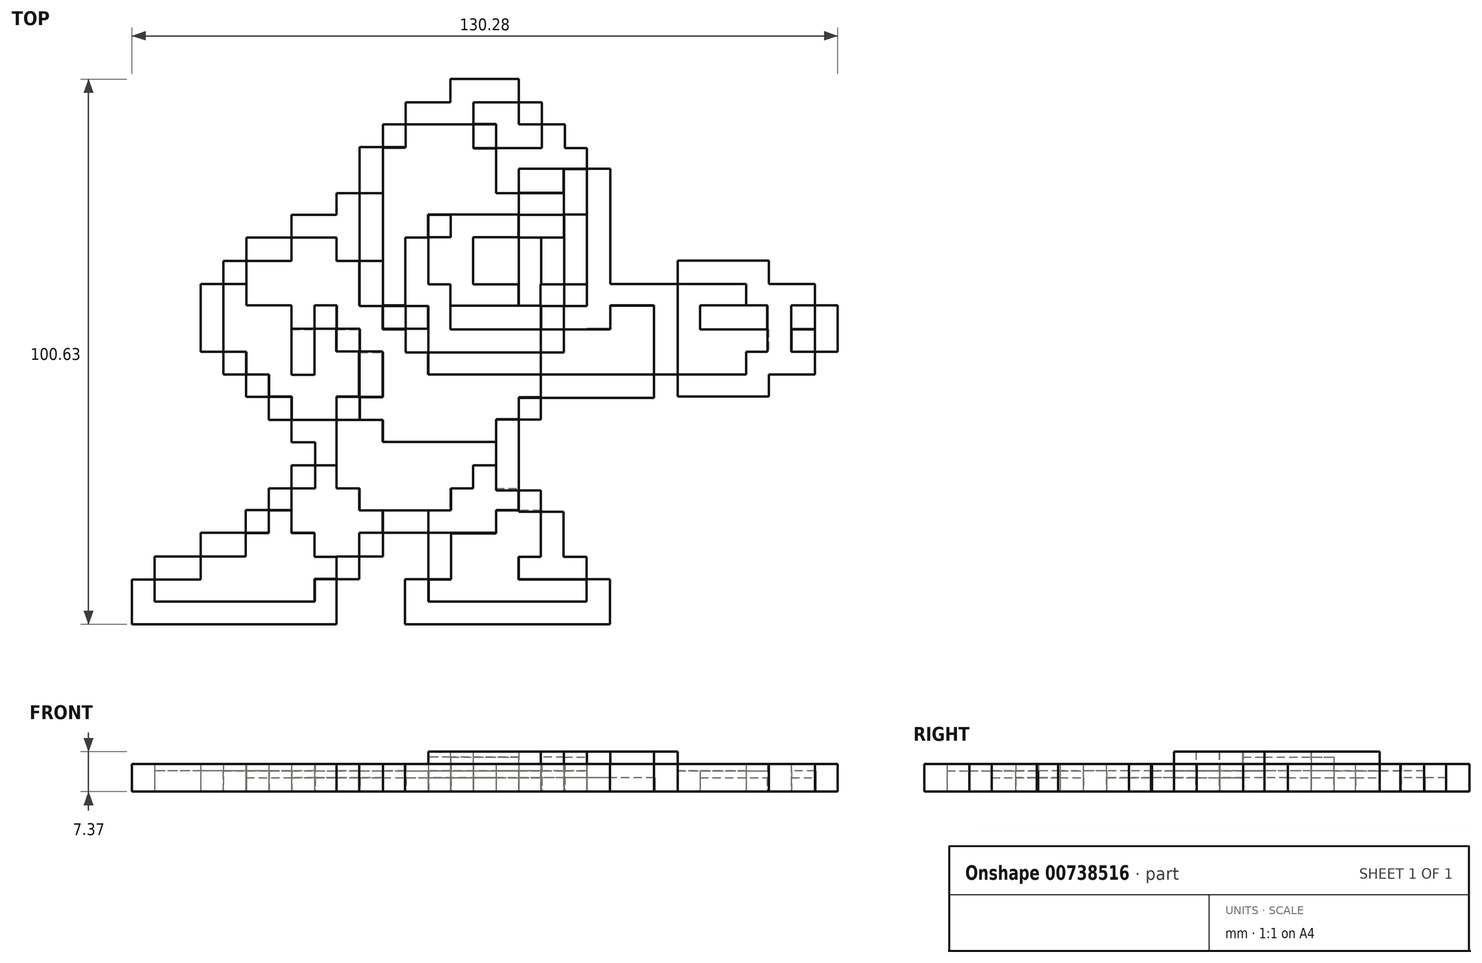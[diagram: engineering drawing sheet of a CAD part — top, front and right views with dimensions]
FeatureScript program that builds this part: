
annotation { "Feature Type Name" : "Feature", "Feature Type Description" : "" }
export const myFeature = defineFeature(function(context is Context, id is Id, definition is map)
    precondition{}
    {
        {
            var Q0;
            Q0=qCreatedBy(makeId("Top.planeOp"),FACE);
            var sketch = newSketch(context, id + "F0", { "sketchPlane" : qUnion([Q0])});
            skLineSegment(sketch, "E0.bottom", {"start": v(-1.86, 51.42) * mm, "end": v(10.8, 51.42) * mm});
            skLineSegment(sketch, "E0.top", {"start": v(-1.86, 47.1) * mm, "end": v(10.8, 47.1) * mm});
            skLineSegment(sketch, "E0.left", {"start": v(-1.86, 51.42) * mm, "end": v(-1.86, 47.1) * mm});
            skLineSegment(sketch, "E0.right", {"start": v(10.8, 51.42) * mm, "end": v(10.8, 47.1) * mm});
            skLineSegment(sketch, "E1.bottom", {"start": v(10.8, 47.1) * mm, "end": v(15.04, 47.1) * mm});
            skLineSegment(sketch, "E1.top", {"start": v(10.8, 43.08) * mm, "end": v(15.04, 43.08) * mm});
            skLineSegment(sketch, "E1.left", {"start": v(10.8, 47.1) * mm, "end": v(10.8, 43.08) * mm});
            skLineSegment(sketch, "E1.right", {"start": v(15.04, 47.1) * mm, "end": v(15.04, 43.08) * mm});
            skLineSegment(sketch, "E2.bottom", {"start": v(15.04, 43.08) * mm, "end": v(19.28, 43.08) * mm});
            skLineSegment(sketch, "E2.top", {"start": v(15.04, 38.7) * mm, "end": v(19.28, 38.7) * mm});
            skLineSegment(sketch, "E2.left", {"start": v(15.04, 43.08) * mm, "end": v(15.04, 38.7) * mm});
            skLineSegment(sketch, "E2.right", {"start": v(19.28, 43.08) * mm, "end": v(19.28, 38.7) * mm});
            skLineSegment(sketch, "E3.bottom", {"start": v(23.38, 38.7) * mm, "end": v(6.63, 38.7) * mm});
            skLineSegment(sketch, "E3.top", {"start": v(23.38, 34.9) * mm, "end": v(6.63, 34.9) * mm});
            skLineSegment(sketch, "E3.left", {"start": v(23.38, 38.7) * mm, "end": v(23.38, 34.9) * mm});
            skLineSegment(sketch, "E3.right", {"start": v(6.63, 38.7) * mm, "end": v(6.63, 34.9) * mm});
            skLineSegment(sketch, "E4.bottom", {"start": v(23.38, 34.9) * mm, "end": v(27.66, 34.9) * mm});
            skLineSegment(sketch, "E4.top", {"start": v(23.38, 5.29) * mm, "end": v(27.66, 5.29) * mm});
            skLineSegment(sketch, "E4.left", {"start": v(23.38, 34.9) * mm, "end": v(23.38, 5.29) * mm});
            skLineSegment(sketch, "E4.right", {"start": v(27.66, 34.9) * mm, "end": v(27.66, 5.29) * mm});
            skLineSegment(sketch, "E5.bottom", {"start": v(27.66, 13.62) * mm, "end": v(40.12, 13.62) * mm});
            skLineSegment(sketch, "E5.top", {"start": v(27.66, 9.67) * mm, "end": v(40.12, 9.67) * mm});
            skLineSegment(sketch, "E5.left", {"start": v(27.66, 13.62) * mm, "end": v(27.66, 9.67) * mm});
            skLineSegment(sketch, "E5.right", {"start": v(40.12, 13.62) * mm, "end": v(40.12, 9.67) * mm});
            skLineSegment(sketch, "E6.bottom", {"start": v(40.12, 13.62) * mm, "end": v(56.96, 13.62) * mm});
            skLineSegment(sketch, "E6.top", {"start": v(40.12, 17.94) * mm, "end": v(56.96, 17.94) * mm});
            skLineSegment(sketch, "E6.left", {"start": v(40.12, 13.62) * mm, "end": v(40.12, 17.94) * mm});
            skLineSegment(sketch, "E6.right", {"start": v(56.96, 13.62) * mm, "end": v(56.96, 17.94) * mm});
            skLineSegment(sketch, "E7.bottom", {"start": v(52.76, 13.62) * mm, "end": v(65.5, 13.62) * mm});
            skLineSegment(sketch, "E7.top", {"start": v(52.76, 9.65) * mm, "end": v(65.5, 9.65) * mm});
            skLineSegment(sketch, "E7.left", {"start": v(52.76, 13.62) * mm, "end": v(52.76, 9.65) * mm});
            skLineSegment(sketch, "E7.right", {"start": v(65.5, 13.62) * mm, "end": v(65.5, 9.65) * mm});
            skLineSegment(sketch, "E8.bottom", {"start": v(65.5, 9.65) * mm, "end": v(69.66, 9.65) * mm});
            skLineSegment(sketch, "E8.top", {"start": v(65.5, 1.07) * mm, "end": v(69.66, 1.07) * mm});
            skLineSegment(sketch, "E8.left", {"start": v(65.5, 9.65) * mm, "end": v(65.5, 1.07) * mm});
            skLineSegment(sketch, "E8.right", {"start": v(69.66, 9.65) * mm, "end": v(69.66, 1.07) * mm});
            skLineSegment(sketch, "E9.bottom", {"start": v(65.5, 1.07) * mm, "end": v(52.76, 1.07) * mm});
            skLineSegment(sketch, "E9.top", {"start": v(65.5, -3.1) * mm, "end": v(52.76, -3.1) * mm});
            skLineSegment(sketch, "E9.left", {"start": v(65.5, 1.07) * mm, "end": v(65.5, -3.1) * mm});
            skLineSegment(sketch, "E9.right", {"start": v(52.76, 1.07) * mm, "end": v(52.76, -3.1) * mm});
            skLineSegment(sketch, "E10.bottom", {"start": v(56.96, -3.1) * mm, "end": v(40.12, -3.1) * mm});
            skLineSegment(sketch, "E10.top", {"start": v(56.96, -7.17) * mm, "end": v(40.12, -7.17) * mm});
            skLineSegment(sketch, "E10.left", {"start": v(56.96, -3.1) * mm, "end": v(56.96, -7.17) * mm});
            skLineSegment(sketch, "E10.right", {"start": v(40.12, -3.1) * mm, "end": v(40.12, -7.17) * mm});
            skLineSegment(sketch, "E11.bottom", {"start": v(40.12, -3.1) * mm, "end": v(35.78, -3.1) * mm});
            skLineSegment(sketch, "E11.top", {"start": v(40.12, 9.67) * mm, "end": v(35.78, 9.67) * mm});
            skLineSegment(sketch, "E11.left", {"start": v(40.12, -3.1) * mm, "end": v(40.12, 9.67) * mm});
            skLineSegment(sketch, "E11.right", {"start": v(35.78, -3.1) * mm, "end": v(35.78, 9.67) * mm});
            skLineSegment(sketch, "E12.bottom", {"start": v(35.78, -3.1) * mm, "end": v(14.88, -3.1) * mm});
            skLineSegment(sketch, "E12.top", {"start": v(35.78, -7.38) * mm, "end": v(14.88, -7.38) * mm});
            skLineSegment(sketch, "E12.left", {"start": v(35.78, -3.1) * mm, "end": v(35.78, -7.38) * mm});
            skLineSegment(sketch, "E12.right", {"start": v(14.88, -3.1) * mm, "end": v(14.88, -7.38) * mm});
            skLineSegment(sketch, "E13.bottom", {"start": v(14.88, -7.38) * mm, "end": v(10.8, -7.38) * mm});
            skLineSegment(sketch, "E13.top", {"start": v(14.88, -11.41) * mm, "end": v(10.8, -11.41) * mm});
            skLineSegment(sketch, "E13.left", {"start": v(14.88, -7.38) * mm, "end": v(14.88, -11.41) * mm});
            skLineSegment(sketch, "E13.right", {"start": v(10.8, -7.38) * mm, "end": v(10.8, -11.41) * mm});
            skLineSegment(sketch, "E14.bottom", {"start": v(10.8, -11.41) * mm, "end": v(6.62, -11.41) * mm});
            skLineSegment(sketch, "E14.top", {"start": v(10.8, -24.48) * mm, "end": v(6.62, -24.48) * mm});
            skLineSegment(sketch, "E14.left", {"start": v(10.8, -11.41) * mm, "end": v(10.8, -24.48) * mm});
            skLineSegment(sketch, "E14.right", {"start": v(6.62, -11.41) * mm, "end": v(6.62, -24.48) * mm});
            skLineSegment(sketch, "E15.bottom", {"start": v(10.8, -24.48) * mm, "end": v(14.88, -24.48) * mm});
            skLineSegment(sketch, "E15.top", {"start": v(10.8, -28.42) * mm, "end": v(14.88, -28.42) * mm});
            skLineSegment(sketch, "E15.left", {"start": v(10.8, -24.48) * mm, "end": v(10.8, -28.42) * mm});
            skLineSegment(sketch, "E15.right", {"start": v(14.88, -24.48) * mm, "end": v(14.88, -28.42) * mm});
            skLineSegment(sketch, "E16.bottom", {"start": v(14.88, -28.42) * mm, "end": v(19.08, -28.42) * mm});
            skLineSegment(sketch, "E16.top", {"start": v(14.88, -40.86) * mm, "end": v(19.08, -40.86) * mm});
            skLineSegment(sketch, "E16.left", {"start": v(14.88, -28.42) * mm, "end": v(14.88, -40.86) * mm});
            skLineSegment(sketch, "E16.right", {"start": v(19.08, -28.42) * mm, "end": v(19.08, -40.86) * mm});
            skLineSegment(sketch, "E17.bottom", {"start": v(10.8, -36.74) * mm, "end": v(23.28, -36.74) * mm});
            skLineSegment(sketch, "E17.top", {"start": v(10.8, -40.86) * mm, "end": v(23.28, -40.86) * mm});
            skLineSegment(sketch, "E17.left", {"start": v(10.8, -36.74) * mm, "end": v(10.8, -40.86) * mm});
            skLineSegment(sketch, "E17.right", {"start": v(23.28, -36.74) * mm, "end": v(23.28, -40.86) * mm});
            skLineSegment(sketch, "E18.bottom", {"start": v(23.28, -40.86) * mm, "end": v(27.63, -40.86) * mm});
            skLineSegment(sketch, "E18.top", {"start": v(23.28, -49.2) * mm, "end": v(27.63, -49.2) * mm});
            skLineSegment(sketch, "E18.left", {"start": v(23.28, -40.86) * mm, "end": v(23.28, -49.2) * mm});
            skLineSegment(sketch, "E18.right", {"start": v(27.63, -40.86) * mm, "end": v(27.63, -49.2) * mm});
            skLineSegment(sketch, "E19.bottom", {"start": v(23.28, -45.03) * mm, "end": v(-10.2, -45.03) * mm});
            skLineSegment(sketch, "E19.top", {"start": v(23.28, -49.2) * mm, "end": v(-10.2, -49.2) * mm});
            skLineSegment(sketch, "E19.left", {"start": v(23.28, -45.03) * mm, "end": v(23.28, -49.2) * mm});
            skLineSegment(sketch, "E19.right", {"start": v(-10.2, -45.03) * mm, "end": v(-10.2, -49.2) * mm});
            skLineSegment(sketch, "E20.bottom", {"start": v(-10.2, -45.03) * mm, "end": v(-5.92, -45.03) * mm});
            skLineSegment(sketch, "E20.top", {"start": v(-10.2, -40.86) * mm, "end": v(-5.92, -40.86) * mm});
            skLineSegment(sketch, "E20.left", {"start": v(-10.2, -45.03) * mm, "end": v(-10.2, -40.86) * mm});
            skLineSegment(sketch, "E20.right", {"start": v(-5.92, -45.03) * mm, "end": v(-5.92, -40.86) * mm});
            skLineSegment(sketch, "E21.bottom", {"start": v(-5.92, -40.86) * mm, "end": v(-1.73, -40.86) * mm});
            skLineSegment(sketch, "E21.top", {"start": v(-5.92, -32.3) * mm, "end": v(-1.73, -32.3) * mm});
            skLineSegment(sketch, "E21.left", {"start": v(-5.92, -40.86) * mm, "end": v(-5.92, -32.3) * mm});
            skLineSegment(sketch, "E21.right", {"start": v(-1.73, -40.86) * mm, "end": v(-1.73, -32.3) * mm});
            skLineSegment(sketch, "E22.bottom", {"start": v(-5.92, -32.3) * mm, "end": v(-14.29, -32.3) * mm});
            skLineSegment(sketch, "E22.top", {"start": v(-5.92, -28.2) * mm, "end": v(-14.29, -28.2) * mm});
            skLineSegment(sketch, "E22.left", {"start": v(-5.92, -32.3) * mm, "end": v(-5.92, -28.2) * mm});
            skLineSegment(sketch, "E22.right", {"start": v(-14.29, -32.3) * mm, "end": v(-14.29, -28.2) * mm});
            skLineSegment(sketch, "E23.bottom", {"start": v(-14.29, -32.3) * mm, "end": v(-18.67, -32.3) * mm});
            skLineSegment(sketch, "E23.top", {"start": v(-14.29, -36.7) * mm, "end": v(-18.67, -36.7) * mm});
            skLineSegment(sketch, "E23.left", {"start": v(-14.29, -32.3) * mm, "end": v(-14.29, -36.7) * mm});
            skLineSegment(sketch, "E23.right", {"start": v(-18.67, -32.3) * mm, "end": v(-18.67, -36.7) * mm});
            skLineSegment(sketch, "E24.bottom", {"start": v(-18.67, -36.7) * mm, "end": v(-22.84, -36.7) * mm});
            skLineSegment(sketch, "E24.top", {"start": v(-18.67, -40.86) * mm, "end": v(-22.84, -40.86) * mm});
            skLineSegment(sketch, "E24.left", {"start": v(-18.67, -36.7) * mm, "end": v(-18.67, -40.86) * mm});
            skLineSegment(sketch, "E24.right", {"start": v(-22.84, -36.7) * mm, "end": v(-22.84, -40.86) * mm});
            skLineSegment(sketch, "E25.bottom", {"start": v(-22.84, -40.86) * mm, "end": v(-26.85, -40.86) * mm});
            skLineSegment(sketch, "E25.top", {"start": v(-22.84, -49.2) * mm, "end": v(-26.85, -49.2) * mm});
            skLineSegment(sketch, "E25.left", {"start": v(-22.84, -40.86) * mm, "end": v(-22.84, -49.2) * mm});
            skLineSegment(sketch, "E25.right", {"start": v(-26.85, -40.86) * mm, "end": v(-26.85, -49.2) * mm});
            skLineSegment(sketch, "E26.bottom", {"start": v(-26.85, -49.2) * mm, "end": v(-60.62, -49.2) * mm});
            skLineSegment(sketch, "E26.top", {"start": v(-26.85, -45.03) * mm, "end": v(-60.62, -45.03) * mm});
            skLineSegment(sketch, "E26.left", {"start": v(-26.85, -49.2) * mm, "end": v(-26.85, -45.03) * mm});
            skLineSegment(sketch, "E26.right", {"start": v(-60.62, -49.2) * mm, "end": v(-60.62, -45.03) * mm});
            skLineSegment(sketch, "E27.bottom", {"start": v(-60.62, -45.03) * mm, "end": v(-56.45, -45.03) * mm});
            skLineSegment(sketch, "E27.top", {"start": v(-60.62, -40.91) * mm, "end": v(-56.45, -40.91) * mm});
            skLineSegment(sketch, "E27.left", {"start": v(-60.62, -45.03) * mm, "end": v(-60.62, -40.91) * mm});
            skLineSegment(sketch, "E27.right", {"start": v(-56.45, -45.03) * mm, "end": v(-56.45, -40.91) * mm});
            skLineSegment(sketch, "E28.bottom", {"start": v(-56.45, -40.91) * mm, "end": v(-47.92, -40.91) * mm});
            skLineSegment(sketch, "E28.top", {"start": v(-56.45, -36.66) * mm, "end": v(-47.92, -36.66) * mm});
            skLineSegment(sketch, "E28.left", {"start": v(-56.45, -40.91) * mm, "end": v(-56.45, -36.66) * mm});
            skLineSegment(sketch, "E28.right", {"start": v(-47.92, -40.91) * mm, "end": v(-47.92, -36.66) * mm});
            skLineSegment(sketch, "E29.bottom", {"start": v(-47.92, -36.66) * mm, "end": v(-39.62, -36.66) * mm});
            skLineSegment(sketch, "E29.top", {"start": v(-47.92, -32.3) * mm, "end": v(-39.62, -32.3) * mm});
            skLineSegment(sketch, "E29.left", {"start": v(-47.92, -36.66) * mm, "end": v(-47.92, -32.3) * mm});
            skLineSegment(sketch, "E29.right", {"start": v(-39.62, -36.66) * mm, "end": v(-39.62, -32.3) * mm});
            skLineSegment(sketch, "E30.bottom", {"start": v(-39.62, -32.3) * mm, "end": v(-35.38, -32.3) * mm});
            skLineSegment(sketch, "E30.top", {"start": v(-39.62, -28.14) * mm, "end": v(-35.38, -28.14) * mm});
            skLineSegment(sketch, "E30.left", {"start": v(-39.62, -32.3) * mm, "end": v(-39.62, -28.14) * mm});
            skLineSegment(sketch, "E30.right", {"start": v(-35.38, -32.3) * mm, "end": v(-35.38, -28.14) * mm});
            skLineSegment(sketch, "E31.bottom", {"start": v(-35.38, -28.14) * mm, "end": v(-31.17, -28.14) * mm});
            skLineSegment(sketch, "E31.top", {"start": v(-35.38, -24.12) * mm, "end": v(-31.17, -24.12) * mm});
            skLineSegment(sketch, "E31.left", {"start": v(-35.38, -28.14) * mm, "end": v(-35.38, -24.12) * mm});
            skLineSegment(sketch, "E31.right", {"start": v(-31.17, -28.14) * mm, "end": v(-31.17, -24.12) * mm});
            skLineSegment(sketch, "E32.bottom", {"start": v(-31.17, -24.12) * mm, "end": v(-26.82, -24.12) * mm});
            skLineSegment(sketch, "E32.top", {"start": v(-31.17, -19.84) * mm, "end": v(-26.82, -19.84) * mm});
            skLineSegment(sketch, "E32.left", {"start": v(-31.17, -24.12) * mm, "end": v(-31.17, -19.84) * mm});
            skLineSegment(sketch, "E32.right", {"start": v(-26.82, -24.12) * mm, "end": v(-26.82, -19.84) * mm});
            skLineSegment(sketch, "E33.bottom", {"start": v(-26.82, -19.84) * mm, "end": v(-22.88, -19.84) * mm});
            skLineSegment(sketch, "E33.top", {"start": v(-26.82, -11.45) * mm, "end": v(-22.88, -11.45) * mm});
            skLineSegment(sketch, "E33.left", {"start": v(-26.82, -19.84) * mm, "end": v(-26.82, -11.45) * mm});
            skLineSegment(sketch, "E33.right", {"start": v(-22.88, -19.84) * mm, "end": v(-22.88, -11.45) * mm});
            skLineSegment(sketch, "E34.bottom", {"start": v(-26.82, -11.45) * mm, "end": v(-31.17, -11.45) * mm});
            skLineSegment(sketch, "E34.top", {"start": v(-26.82, -15.62) * mm, "end": v(-31.17, -15.62) * mm});
            skLineSegment(sketch, "E34.left", {"start": v(-26.82, -11.45) * mm, "end": v(-26.82, -15.62) * mm});
            skLineSegment(sketch, "E34.right", {"start": v(-31.17, -11.45) * mm, "end": v(-31.17, -15.62) * mm});
            skLineSegment(sketch, "E35.bottom", {"start": v(-31.17, -11.45) * mm, "end": v(-35.39, -11.45) * mm});
            skLineSegment(sketch, "E35.top", {"start": v(-31.17, -7.24) * mm, "end": v(-35.39, -7.24) * mm});
            skLineSegment(sketch, "E35.left", {"start": v(-31.17, -11.45) * mm, "end": v(-31.17, -7.24) * mm});
            skLineSegment(sketch, "E35.right", {"start": v(-35.39, -11.45) * mm, "end": v(-35.39, -7.24) * mm});
            skLineSegment(sketch, "E36.bottom", {"start": v(-35.39, -7.24) * mm, "end": v(-39.58, -7.24) * mm});
            skLineSegment(sketch, "E36.top", {"start": v(-35.39, -3.08) * mm, "end": v(-39.58, -3.08) * mm});
            skLineSegment(sketch, "E36.left", {"start": v(-35.39, -7.24) * mm, "end": v(-35.39, -3.08) * mm});
            skLineSegment(sketch, "E36.right", {"start": v(-39.58, -7.24) * mm, "end": v(-39.58, -3.08) * mm});
            skLineSegment(sketch, "E37.bottom", {"start": v(-39.58, -3.08) * mm, "end": v(-43.75, -3.08) * mm});
            skLineSegment(sketch, "E37.top", {"start": v(-39.58, 1.12) * mm, "end": v(-43.75, 1.12) * mm});
            skLineSegment(sketch, "E37.left", {"start": v(-39.58, -3.08) * mm, "end": v(-39.58, 1.12) * mm});
            skLineSegment(sketch, "E37.right", {"start": v(-43.75, -3.08) * mm, "end": v(-43.75, 1.12) * mm});
            skLineSegment(sketch, "E38.bottom", {"start": v(-43.75, 1.12) * mm, "end": v(-47.94, 1.12) * mm});
            skLineSegment(sketch, "E38.top", {"start": v(-43.75, 13.63) * mm, "end": v(-47.94, 13.63) * mm});
            skLineSegment(sketch, "E38.left", {"start": v(-43.75, 1.12) * mm, "end": v(-43.75, 13.63) * mm});
            skLineSegment(sketch, "E38.right", {"start": v(-47.94, 1.12) * mm, "end": v(-47.94, 13.63) * mm});
            skLineSegment(sketch, "E39.bottom", {"start": v(-43.75, 13.63) * mm, "end": v(-39.52, 13.63) * mm});
            skLineSegment(sketch, "E39.top", {"start": v(-43.75, 17.83) * mm, "end": v(-39.52, 17.83) * mm});
            skLineSegment(sketch, "E39.left", {"start": v(-43.75, 13.63) * mm, "end": v(-43.75, 17.83) * mm});
            skLineSegment(sketch, "E39.right", {"start": v(-39.52, 13.63) * mm, "end": v(-39.52, 17.83) * mm});
            skLineSegment(sketch, "E40.bottom", {"start": v(-39.52, 17.83) * mm, "end": v(-31.19, 17.83) * mm});
            skLineSegment(sketch, "E40.top", {"start": v(-39.52, 22.2) * mm, "end": v(-31.19, 22.2) * mm});
            skLineSegment(sketch, "E40.left", {"start": v(-39.52, 17.83) * mm, "end": v(-39.52, 22.2) * mm});
            skLineSegment(sketch, "E40.right", {"start": v(-31.19, 17.83) * mm, "end": v(-31.19, 22.2) * mm});
            skLineSegment(sketch, "E41.bottom", {"start": v(-31.19, 22.2) * mm, "end": v(-18.62, 22.2) * mm});
            skLineSegment(sketch, "E41.top", {"start": v(-31.19, 26.36) * mm, "end": v(-18.62, 26.36) * mm});
            skLineSegment(sketch, "E41.left", {"start": v(-31.19, 22.2) * mm, "end": v(-31.19, 26.36) * mm});
            skLineSegment(sketch, "E41.right", {"start": v(-18.62, 22.2) * mm, "end": v(-18.62, 26.36) * mm});
            skLineSegment(sketch, "E42.bottom", {"start": v(-18.62, 17.83) * mm, "end": v(-22.83, 17.83) * mm});
            skLineSegment(sketch, "E42.top", {"start": v(-18.62, 30.38) * mm, "end": v(-22.83, 30.38) * mm});
            skLineSegment(sketch, "E42.left", {"start": v(-18.62, 17.83) * mm, "end": v(-18.62, 30.38) * mm});
            skLineSegment(sketch, "E42.right", {"start": v(-22.83, 17.83) * mm, "end": v(-22.83, 30.38) * mm});
            skLineSegment(sketch, "E43.bottom", {"start": v(-18.62, 30.38) * mm, "end": v(-14.27, 30.38) * mm});
            skLineSegment(sketch, "E43.top", {"start": v(-18.62, 38.86) * mm, "end": v(-14.27, 38.86) * mm});
            skLineSegment(sketch, "E43.left", {"start": v(-18.62, 30.38) * mm, "end": v(-18.62, 38.86) * mm});
            skLineSegment(sketch, "E43.right", {"start": v(-14.27, 30.38) * mm, "end": v(-14.27, 38.86) * mm});
            skLineSegment(sketch, "E44.bottom", {"start": v(-14.27, 38.86) * mm, "end": v(-10.1, 38.86) * mm});
            skLineSegment(sketch, "E44.top", {"start": v(-14.27, 43.08) * mm, "end": v(-10.1, 43.08) * mm});
            skLineSegment(sketch, "E44.left", {"start": v(-14.27, 38.86) * mm, "end": v(-14.27, 43.08) * mm});
            skLineSegment(sketch, "E44.right", {"start": v(-10.1, 38.86) * mm, "end": v(-10.1, 43.08) * mm});
            skLineSegment(sketch, "E45.bottom", {"start": v(-10.1, 43.08) * mm, "end": v(2.42, 43.08) * mm});
            skLineSegment(sketch, "E45.top", {"start": v(-10.1, 47.1) * mm, "end": v(2.42, 47.1) * mm});
            skLineSegment(sketch, "E45.left", {"start": v(-10.1, 43.08) * mm, "end": v(-10.1, 47.1) * mm});
            skLineSegment(sketch, "E45.right", {"start": v(2.42, 43.08) * mm, "end": v(2.42, 47.1) * mm});
            skLineSegment(sketch, "E46.bottom", {"start": v(2.42, 43.08) * mm, "end": v(6.63, 43.08) * mm});
            skLineSegment(sketch, "E46.top", {"start": v(2.42, 38.7) * mm, "end": v(6.63, 38.7) * mm});
            skLineSegment(sketch, "E46.left", {"start": v(2.42, 43.08) * mm, "end": v(2.42, 38.7) * mm});
            skLineSegment(sketch, "E46.right", {"start": v(6.63, 43.08) * mm, "end": v(6.63, 38.7) * mm});
            skLineSegment(sketch, "E47.bottom", {"start": v(6.63, 34.9) * mm, "end": v(10.8, 34.9) * mm});
            skLineSegment(sketch, "E47.top", {"start": v(6.63, 30.38) * mm, "end": v(10.8, 30.38) * mm});
            skLineSegment(sketch, "E47.left", {"start": v(6.63, 34.9) * mm, "end": v(6.63, 30.38) * mm});
            skLineSegment(sketch, "E47.right", {"start": v(10.8, 34.9) * mm, "end": v(10.8, 30.38) * mm});
            skLineSegment(sketch, "E48.bottom", {"start": v(10.8, 30.38) * mm, "end": v(19.1, 30.38) * mm});
            skLineSegment(sketch, "E48.top", {"start": v(10.8, 26.36) * mm, "end": v(19.1, 26.36) * mm});
            skLineSegment(sketch, "E48.left", {"start": v(10.8, 30.38) * mm, "end": v(10.8, 26.36) * mm});
            skLineSegment(sketch, "E48.right", {"start": v(19.1, 30.38) * mm, "end": v(19.1, 26.36) * mm});
            skLineSegment(sketch, "E49.bottom", {"start": v(-22.88, -11.45) * mm, "end": v(-18.63, -11.45) * mm});
            skLineSegment(sketch, "E49.top", {"start": v(-22.88, -7.25) * mm, "end": v(-18.63, -7.25) * mm});
            skLineSegment(sketch, "E49.left", {"start": v(-22.88, -11.45) * mm, "end": v(-22.88, -7.25) * mm});
            skLineSegment(sketch, "E49.right", {"start": v(-18.63, -11.45) * mm, "end": v(-18.63, -7.25) * mm});
            skLineSegment(sketch, "E50.bottom", {"start": v(-18.63, -7.25) * mm, "end": v(-14.35, -7.25) * mm});
            skLineSegment(sketch, "E50.top", {"start": v(-18.63, 1.16) * mm, "end": v(-14.35, 1.16) * mm});
            skLineSegment(sketch, "E50.left", {"start": v(-18.63, -7.25) * mm, "end": v(-18.63, 1.16) * mm});
            skLineSegment(sketch, "E50.right", {"start": v(-14.35, -7.25) * mm, "end": v(-14.35, 1.16) * mm});
            skLineSegment(sketch, "E51.bottom", {"start": v(-18.63, 1.16) * mm, "end": v(-22.88, 1.16) * mm});
            skLineSegment(sketch, "E51.top", {"start": v(-18.63, 5.32) * mm, "end": v(-22.88, 5.32) * mm});
            skLineSegment(sketch, "E51.left", {"start": v(-18.63, 1.16) * mm, "end": v(-18.63, 5.32) * mm});
            skLineSegment(sketch, "E51.right", {"start": v(-22.88, 1.16) * mm, "end": v(-22.88, 5.32) * mm});
            skLineSegment(sketch, "E52.bottom", {"start": v(-22.88, 5.32) * mm, "end": v(-26.89, 5.32) * mm});
            skLineSegment(sketch, "E52.top", {"start": v(-22.88, 9.7) * mm, "end": v(-26.89, 9.7) * mm});
            skLineSegment(sketch, "E52.left", {"start": v(-22.88, 5.32) * mm, "end": v(-22.88, 9.7) * mm});
            skLineSegment(sketch, "E52.right", {"start": v(-26.89, 5.32) * mm, "end": v(-26.89, 9.7) * mm});
            skLineSegment(sketch, "E53.bottom", {"start": v(-26.89, 5.32) * mm, "end": v(-31.18, 5.32) * mm});
            skLineSegment(sketch, "E53.top", {"start": v(-26.89, -3.15) * mm, "end": v(-31.18, -3.15) * mm});
            skLineSegment(sketch, "E53.left", {"start": v(-26.89, 5.32) * mm, "end": v(-26.89, -3.15) * mm});
            skLineSegment(sketch, "E53.right", {"start": v(-31.18, 5.32) * mm, "end": v(-31.18, -3.15) * mm});
            skLineSegment(sketch, "E54.bottom", {"start": v(-18.62, 17.83) * mm, "end": v(-14.3, 17.83) * mm});
            skLineSegment(sketch, "E54.top", {"start": v(-18.62, 9.56) * mm, "end": v(-14.3, 9.56) * mm});
            skLineSegment(sketch, "E54.left", {"start": v(-18.62, 17.83) * mm, "end": v(-18.62, 9.56) * mm});
            skLineSegment(sketch, "E54.right", {"start": v(-14.3, 17.83) * mm, "end": v(-14.3, 9.56) * mm});
            skLineSegment(sketch, "E55.bottom", {"start": v(-14.3, 9.56) * mm, "end": v(-10.1, 9.56) * mm});
            skLineSegment(sketch, "E55.top", {"start": v(-14.3, 5.32) * mm, "end": v(-10.1, 5.32) * mm});
            skLineSegment(sketch, "E55.left", {"start": v(-14.3, 9.56) * mm, "end": v(-14.3, 5.32) * mm});
            skLineSegment(sketch, "E55.right", {"start": v(-10.1, 9.56) * mm, "end": v(-10.1, 5.32) * mm});
            skLineSegment(sketch, "E56.bottom", {"start": v(-10.1, 5.32) * mm, "end": v(-5.92, 5.32) * mm});
            skLineSegment(sketch, "E56.top", {"start": v(-10.1, 0.94) * mm, "end": v(-5.92, 0.94) * mm});
            skLineSegment(sketch, "E56.left", {"start": v(-10.1, 5.32) * mm, "end": v(-10.1, 0.94) * mm});
            skLineSegment(sketch, "E56.right", {"start": v(-5.92, 5.32) * mm, "end": v(-5.92, 0.94) * mm});
            skLineSegment(sketch, "E57.bottom", {"start": v(-5.92, 0.94) * mm, "end": v(14.88, 0.94) * mm});
            skLineSegment(sketch, "E57.top", {"start": v(-5.92, -3.1) * mm, "end": v(14.88, -3.1) * mm});
            skLineSegment(sketch, "E57.left", {"start": v(-5.92, 0.94) * mm, "end": v(-5.92, -3.1) * mm});
            skLineSegment(sketch, "E57.right", {"start": v(14.88, 0.94) * mm, "end": v(14.88, -3.1) * mm});
            skLineSegment(sketch, "E58.bottom", {"start": v(14.88, 0.94) * mm, "end": v(19.1, 0.94) * mm});
            skLineSegment(sketch, "E58.top", {"start": v(14.88, 5.23) * mm, "end": v(19.1, 5.23) * mm});
            skLineSegment(sketch, "E58.left", {"start": v(14.88, 0.94) * mm, "end": v(14.88, 5.23) * mm});
            skLineSegment(sketch, "E58.right", {"start": v(19.1, 0.94) * mm, "end": v(19.1, 5.23) * mm});
            skLineSegment(sketch, "E59.bottom", {"start": v(19.1, 5.23) * mm, "end": v(23.38, 5.23) * mm});
            skLineSegment(sketch, "E59.top", {"start": v(19.1, 9.56) * mm, "end": v(23.38, 9.56) * mm});
            skLineSegment(sketch, "E59.left", {"start": v(19.1, 5.23) * mm, "end": v(19.1, 9.56) * mm});
            skLineSegment(sketch, "E59.right", {"start": v(23.38, 5.23) * mm, "end": v(23.38, 9.56) * mm});
            skLineSegment(sketch, "E60.bottom", {"start": v(56.7, 9.65) * mm, "end": v(61.12, 9.65) * mm});
            skLineSegment(sketch, "E60.top", {"start": v(56.7, 1.07) * mm, "end": v(61.12, 1.07) * mm});
            skLineSegment(sketch, "E60.left", {"start": v(56.7, 9.65) * mm, "end": v(56.7, 1.07) * mm});
            skLineSegment(sketch, "E60.right", {"start": v(61.12, 9.65) * mm, "end": v(61.12, 1.07) * mm});
            skLineSegment(sketch, "E61.bottom", {"start": v(2.34, 22.24) * mm, "end": v(10.8, 22.24) * mm});
            skLineSegment(sketch, "E61.top", {"start": v(2.34, 13.56) * mm, "end": v(10.8, 13.56) * mm});
            skLineSegment(sketch, "E61.left", {"start": v(2.34, 22.24) * mm, "end": v(2.34, 13.56) * mm});
            skLineSegment(sketch, "E61.right", {"start": v(10.8, 22.24) * mm, "end": v(10.8, 13.56) * mm});
            skLineSegment(sketch, "E62.bottom", {"start": v(14.91, 22.15) * mm, "end": v(19.2, 22.15) * mm});
            skLineSegment(sketch, "E62.top", {"start": v(14.91, 13.56) * mm, "end": v(19.2, 13.56) * mm});
            skLineSegment(sketch, "E62.left", {"start": v(14.91, 22.15) * mm, "end": v(14.91, 13.56) * mm});
            skLineSegment(sketch, "E62.right", {"start": v(19.2, 22.15) * mm, "end": v(19.2, 13.56) * mm});
            skLineSegment(sketch, "E63.bottom", {"start": v(14.88, 5.23) * mm, "end": v(-1.82, 5.23) * mm});
            skLineSegment(sketch, "E63.top", {"start": v(14.88, 9.62) * mm, "end": v(-1.82, 9.62) * mm});
            skLineSegment(sketch, "E63.left", {"start": v(14.88, 5.23) * mm, "end": v(14.88, 9.62) * mm});
            skLineSegment(sketch, "E63.right", {"start": v(-1.82, 5.23) * mm, "end": v(-1.82, 9.62) * mm});
            skSolve(sketch);
        }
        {
            var Q0;
            Q0=makeQuery(id+"F0.imprint","IMPRINT",FACE,{"disambiguationData":[TD([[makeQuery(id+"F0.imprint","IMPRINT",EDGE,{"derivedFrom":sQuery(id+"F0.wireOp",EDGE,"E12.bottom")}),1.0]])]});
            var Q1;
            Q1=makeQuery(id+"F0.imprint","IMPRINT",FACE,{"disambiguationData":[TD([[makeQuery(id+"F0.imprint","IMPRINT",EDGE,{"derivedFrom":sQuery(id+"F0.wireOp",EDGE,"E40.bottom")}),1.0]])]});
            var Q2;
            {var subQ1=sQuery(id+"F0.wireOp",EDGE,"E41.right");Q2=makeQuery(id+"F0.imprint","IMPRINT",FACE,{"disambiguationData":[TD([[makeQuery(id+"F0.imprint","IMPRINT",EDGE,{"derivedFrom":subQ1}),1.0]])]});}
            var Q3;
            {var subQ0=sQuery(id+"F0.wireOp",EDGE,"E60.left");Q3=makeQuery(id+"F0.imprint","IMPRINT",FACE,{"disambiguationData":[TD([[makeQuery(id+"F0.imprint","IMPRINT",EDGE,{"derivedFrom":subQ0}),1.0]])]});}
            var Q4;
            {var subQ0=sQuery(id+"F0.wireOp",EDGE,"E16.bottom");Q4=makeQuery(id+"F0.imprint","IMPRINT",FACE,{"disambiguationData":[TD([[makeQuery(id+"F0.imprint","IMPRINT",EDGE,{"derivedFrom":subQ0}),-1.0]])]});}
            var Q5;
            Q5=makeQuery(id+"F0.imprint","IMPRINT",FACE,{"disambiguationData":[TD([[makeQuery(id+"F0.imprint","IMPRINT",EDGE,{"derivedFrom":sQuery(id+"F0.wireOp",EDGE,"E43.bottom")}),1.0]])]});
            var Q6;
            Q6=makeQuery(id+"F0.imprint","IMPRINT",FACE,{"disambiguationData":[TD([[makeQuery(id+"F0.imprint","IMPRINT",EDGE,{"derivedFrom":sQuery(id+"F0.wireOp",EDGE,"E11.bottom")}),-1.0]])]});
            var Q7;
            {var subQ5=sQuery(id+"F0.wireOp",EDGE,"E17.left");Q7=makeQuery(id+"F0.imprint","IMPRINT",FACE,{"disambiguationData":[TD([[makeQuery(id+"F0.imprint","IMPRINT",EDGE,{"derivedFrom":subQ5}),1.0]])]});}
            var Q8;
            Q8=makeQuery(id+"F0.imprint","IMPRINT",FACE,{"disambiguationData":[TD([[makeQuery(id+"F0.imprint","IMPRINT",EDGE,{"derivedFrom":sQuery(id+"F0.wireOp",EDGE,"E44.bottom")}),1.0]])]});
            var Q9;
            {var subQ5=sQuery(id+"F0.wireOp",EDGE,"E17.right");Q9=makeQuery(id+"F0.imprint","IMPRINT",FACE,{"disambiguationData":[TD([[makeQuery(id+"F0.imprint","IMPRINT",EDGE,{"derivedFrom":subQ5}),-1.0]])]});}
            var Q10;
            {var subQ3=sQuery(id+"F0.wireOp",EDGE,"E4.bottom");Q10=makeQuery(id+"F0.imprint","IMPRINT",FACE,{"disambiguationData":[TD([[makeQuery(id+"F0.imprint","IMPRINT",EDGE,{"derivedFrom":subQ3}),-1.0]])]});}
            var Q11;
            Q11=makeQuery(id+"F0.imprint","IMPRINT",FACE,{"disambiguationData":[TD([[makeQuery(id+"F0.imprint","IMPRINT",EDGE,{"derivedFrom":sQuery(id+"F0.wireOp",EDGE,"E48.bottom")}),-1.0]])]});
            var Q12;
            {var subQ0=sQuery(id+"F0.wireOp",EDGE,"E19.top");Q12=makeQuery(id+"F0.imprint","IMPRINT",FACE,{"disambiguationData":[TD([[makeQuery(id+"F0.imprint","IMPRINT",EDGE,{"derivedFrom":subQ0}),-1.0]])]});}
            var Q13;
            {var subQ3=sQuery(id+"F0.wireOp",EDGE,"E18.bottom");Q13=makeQuery(id+"F0.imprint","IMPRINT",FACE,{"disambiguationData":[TD([[makeQuery(id+"F0.imprint","IMPRINT",EDGE,{"derivedFrom":subQ3}),-1.0]])]});}
            var Q14;
            {var subQ5=sQuery(id+"F0.wireOp",EDGE,"E26.bottom");Q14=makeQuery(id+"F0.imprint","IMPRINT",FACE,{"disambiguationData":[TD([[makeQuery(id+"F0.imprint","IMPRINT",EDGE,{"derivedFrom":subQ5}),-1.0]])]});}
            var Q15;
            Q15=makeQuery(id+"F0.imprint","IMPRINT",FACE,{"disambiguationData":[TD([[makeQuery(id+"F0.imprint","IMPRINT",EDGE,{"derivedFrom":sQuery(id+"F0.wireOp",EDGE,"E20.top")}),-1.0]])]});
            var Q16;
            Q16=makeQuery(id+"F0.imprint","IMPRINT",FACE,{"disambiguationData":[TD([[makeQuery(id+"F0.imprint","IMPRINT",EDGE,{"derivedFrom":sQuery(id+"F0.wireOp",EDGE,"E50.bottom")}),1.0]])]});
            var Q17;
            {var subQ5=sQuery(id+"F0.wireOp",EDGE,"E42.bottom");Q17=makeQuery(id+"F0.imprint","IMPRINT",FACE,{"disambiguationData":[TD([[makeQuery(id+"F0.imprint","IMPRINT",EDGE,{"derivedFrom":subQ5}),-1.0]])]});}
            var Q18;
            {var subQ3=sQuery(id+"F0.wireOp",EDGE,"E25.bottom");Q18=makeQuery(id+"F0.imprint","IMPRINT",FACE,{"disambiguationData":[TD([[makeQuery(id+"F0.imprint","IMPRINT",EDGE,{"derivedFrom":subQ3}),1.0]])]});}
            var Q19;
            Q19=makeQuery(id+"F0.imprint","IMPRINT",FACE,{"disambiguationData":[TD([[makeQuery(id+"F0.imprint","IMPRINT",EDGE,{"derivedFrom":sQuery(id+"F0.wireOp",EDGE,"E45.bottom")}),1.0]])]});
            var Q20;
            Q20=makeQuery(id+"F0.imprint","IMPRINT",FACE,{"disambiguationData":[TD([[makeQuery(id+"F0.imprint","IMPRINT",EDGE,{"derivedFrom":sQuery(id+"F0.wireOp",EDGE,"E57.bottom")}),-1.0]])]});
            var Q21;
            {var subQ3=sQuery(id+"F0.wireOp",EDGE,"E33.bottom");Q21=makeQuery(id+"F0.imprint","IMPRINT",FACE,{"disambiguationData":[TD([[makeQuery(id+"F0.imprint","IMPRINT",EDGE,{"derivedFrom":subQ3}),1.0]])]});}
            var Q22;
            {var subQ3=sQuery(id+"F0.wireOp",EDGE,"E7.bottom");Q22=makeQuery(id+"F0.imprint","IMPRINT",FACE,{"disambiguationData":[TD([[makeQuery(id+"F0.imprint","IMPRINT",EDGE,{"derivedFrom":subQ3}),-1.0]])]});}
            var Q23;
            Q23=makeQuery(id+"F0.imprint","IMPRINT",FACE,{"disambiguationData":[TD([[makeQuery(id+"F0.imprint","IMPRINT",EDGE,{"derivedFrom":sQuery(id+"F0.wireOp",EDGE,"E46.bottom")}),-1.0]])]});
            var Q24;
            Q24=makeQuery(id+"F0.imprint","IMPRINT",FACE,{"disambiguationData":[TD([[makeQuery(id+"F0.imprint","IMPRINT",EDGE,{"derivedFrom":sQuery(id+"F0.wireOp",EDGE,"E53.bottom")}),1.0]])]});
            var Q25;
            Q25=makeQuery(id+"F0.imprint","IMPRINT",FACE,{"disambiguationData":[TD([[makeQuery(id+"F0.imprint","IMPRINT",EDGE,{"derivedFrom":sQuery(id+"F0.wireOp",EDGE,"E0.bottom")}),-1.0]])]});
            var Q26;
            {var subQ0=sQuery(id+"F0.wireOp",EDGE,"E34.bottom");Q26=makeQuery(id+"F0.imprint","IMPRINT",FACE,{"disambiguationData":[TD([[makeQuery(id+"F0.imprint","IMPRINT",EDGE,{"derivedFrom":subQ0}),1.0]])]});}
            var Q27;
            Q27=makeQuery(id+"F0.imprint","IMPRINT",FACE,{"disambiguationData":[TD([[makeQuery(id+"F0.imprint","IMPRINT",EDGE,{"derivedFrom":sQuery(id+"F0.wireOp",EDGE,"E61.bottom")}),-1.0]])]});
            var Q28;
            {var subQ0=sQuery(id+"F0.wireOp",EDGE,"E41.left");Q28=makeQuery(id+"F0.imprint","IMPRINT",FACE,{"disambiguationData":[TD([[makeQuery(id+"F0.imprint","IMPRINT",EDGE,{"derivedFrom":subQ0}),-1.0]])]});}
            var Q29;
            Q29=makeQuery(id+"F0.imprint","IMPRINT",FACE,{"disambiguationData":[TD([[makeQuery(id+"F0.imprint","IMPRINT",EDGE,{"derivedFrom":sQuery(id+"F0.wireOp",EDGE,"E62.bottom")}),-1.0]])]});
            var Q30;
            {var subQ1=sQuery(id+"F0.wireOp",EDGE,"E2.top");Q30=makeQuery(id+"F0.imprint","IMPRINT",FACE,{"disambiguationData":[TD([[makeQuery(id+"F0.imprint","IMPRINT",EDGE,{"derivedFrom":subQ1}),-1.0]])]});}
            var Q31;
            {var subQ5=sQuery(id+"F0.wireOp",EDGE,"E5.bottom");Q31=makeQuery(id+"F0.imprint","IMPRINT",FACE,{"disambiguationData":[TD([[makeQuery(id+"F0.imprint","IMPRINT",EDGE,{"derivedFrom":subQ5}),-1.0]])]});}
            var Q32;
            {var subQ5=sQuery(id+"F0.wireOp",EDGE,"E42.top");Q32=makeQuery(id+"F0.imprint","IMPRINT",FACE,{"disambiguationData":[TD([[makeQuery(id+"F0.imprint","IMPRINT",EDGE,{"derivedFrom":subQ5}),1.0]])]});}
            var Q33;
            Q33=makeQuery(id+"F0.imprint","IMPRINT",FACE,{"disambiguationData":[TD([[makeQuery(id+"F0.imprint","IMPRINT",EDGE,{"derivedFrom":sQuery(id+"F0.wireOp",EDGE,"E63.bottom")}),-1.0]])]});
            var Q34;
            Q34=makeQuery(id+"F0.imprint","IMPRINT",FACE,{"disambiguationData":[TD([[makeQuery(id+"F0.imprint","IMPRINT",EDGE,{"derivedFrom":sQuery(id+"F0.wireOp",EDGE,"E2.bottom")}),-1.0]])]});
            var Q35;
            Q35=makeQuery(id+"F0.imprint","IMPRINT",FACE,{"disambiguationData":[TD([[makeQuery(id+"F0.imprint","IMPRINT",EDGE,{"derivedFrom":sQuery(id+"F0.wireOp",EDGE,"E36.bottom")}),-1.0]])]});
            var Q36;
            Q36=makeQuery(id+"F0.imprint","IMPRINT",FACE,{"disambiguationData":[TD([[makeQuery(id+"F0.imprint","IMPRINT",EDGE,{"derivedFrom":sQuery(id+"F0.wireOp",EDGE,"E32.bottom")}),1.0]])]});
            var Q37;
            Q37=makeQuery(id+"F0.imprint","IMPRINT",FACE,{"disambiguationData":[TD([[makeQuery(id+"F0.imprint","IMPRINT",EDGE,{"derivedFrom":sQuery(id+"F0.wireOp",EDGE,"E1.bottom")}),-1.0]])]});
            var Q38;
            Q38=makeQuery(id+"F0.imprint","IMPRINT",FACE,{"disambiguationData":[TD([[makeQuery(id+"F0.imprint","IMPRINT",EDGE,{"derivedFrom":sQuery(id+"F0.wireOp",EDGE,"E8.bottom")}),-1.0]])]});
            var Q39;
            Q39=makeQuery(id+"F0.imprint","IMPRINT",FACE,{"disambiguationData":[TD([[makeQuery(id+"F0.imprint","IMPRINT",EDGE,{"derivedFrom":sQuery(id+"F0.wireOp",EDGE,"E13.bottom")}),1.0]])]});
            var Q40;
            Q40=makeQuery(id+"F0.imprint","IMPRINT",FACE,{"disambiguationData":[TD([[makeQuery(id+"F0.imprint","IMPRINT",EDGE,{"derivedFrom":sQuery(id+"F0.wireOp",EDGE,"E14.bottom")}),1.0]])]});
            var Q41;
            Q41=makeQuery(id+"F0.imprint","IMPRINT",FACE,{"disambiguationData":[TD([[makeQuery(id+"F0.imprint","IMPRINT",EDGE,{"derivedFrom":sQuery(id+"F0.wireOp",EDGE,"E15.bottom")}),-1.0]])]});
            var Q42;
            Q42=makeQuery(id+"F0.imprint","IMPRINT",FACE,{"disambiguationData":[TD([[makeQuery(id+"F0.imprint","IMPRINT",EDGE,{"derivedFrom":sQuery(id+"F0.wireOp",EDGE,"E21.bottom")}),1.0]])]});
            var Q43;
            {var subQ0=sQuery(id+"F0.wireOp",EDGE,"E9.left");Q43=makeQuery(id+"F0.imprint","IMPRINT",FACE,{"disambiguationData":[TD([[makeQuery(id+"F0.imprint","IMPRINT",EDGE,{"derivedFrom":subQ0}),-1.0]])]});}
            var Q44;
            Q44=makeQuery(id+"F0.imprint","IMPRINT",FACE,{"disambiguationData":[TD([[makeQuery(id+"F0.imprint","IMPRINT",EDGE,{"derivedFrom":sQuery(id+"F0.wireOp",EDGE,"E54.bottom")}),-1.0]])]});
            var Q45;
            Q45=makeQuery(id+"F0.imprint","IMPRINT",FACE,{"disambiguationData":[TD([[makeQuery(id+"F0.imprint","IMPRINT",EDGE,{"derivedFrom":sQuery(id+"F0.wireOp",EDGE,"E6.top")}),-1.0]])]});
            var Q46;
            Q46=makeQuery(id+"F0.imprint","IMPRINT",FACE,{"disambiguationData":[TD([[makeQuery(id+"F0.imprint","IMPRINT",EDGE,{"derivedFrom":sQuery(id+"F0.wireOp",EDGE,"E38.bottom")}),-1.0]])]});
            var Q47;
            Q47=makeQuery(id+"F0.imprint","IMPRINT",FACE,{"disambiguationData":[TD([[makeQuery(id+"F0.imprint","IMPRINT",EDGE,{"derivedFrom":sQuery(id+"F0.wireOp",EDGE,"E22.bottom")}),-1.0]])]});
            var Q48;
            Q48=makeQuery(id+"F0.imprint","IMPRINT",FACE,{"disambiguationData":[TD([[makeQuery(id+"F0.imprint","IMPRINT",EDGE,{"derivedFrom":sQuery(id+"F0.wireOp",EDGE,"E28.bottom")}),1.0]])]});
            var Q49;
            Q49=makeQuery(id+"F0.imprint","IMPRINT",FACE,{"disambiguationData":[TD([[makeQuery(id+"F0.imprint","IMPRINT",EDGE,{"derivedFrom":sQuery(id+"F0.wireOp",EDGE,"E29.bottom")}),1.0]])]});
            var Q50;
            Q50=makeQuery(id+"F0.imprint","IMPRINT",FACE,{"disambiguationData":[TD([[makeQuery(id+"F0.imprint","IMPRINT",EDGE,{"derivedFrom":sQuery(id+"F0.wireOp",EDGE,"E30.bottom")}),1.0]])]});
            var Q51;
            {var subQ0=sQuery(id+"F0.wireOp",EDGE,"E16.top");Q51=makeQuery(id+"F0.imprint","IMPRINT",FACE,{"disambiguationData":[TD([[makeQuery(id+"F0.imprint","IMPRINT",EDGE,{"derivedFrom":subQ0}),1.0]])]});}
            var Q52;
            Q52=makeQuery(id+"F0.imprint","IMPRINT",FACE,{"disambiguationData":[TD([[makeQuery(id+"F0.imprint","IMPRINT",EDGE,{"derivedFrom":sQuery(id+"F0.wireOp",EDGE,"E55.bottom")}),-1.0]])]});
            var Q53;
            {var subQ0=sQuery(id+"F0.wireOp",EDGE,"E10.bottom");Q53=makeQuery(id+"F0.imprint","IMPRINT",FACE,{"disambiguationData":[TD([[makeQuery(id+"F0.imprint","IMPRINT",EDGE,{"derivedFrom":subQ0}),1.0]])]});}
            var Q54;
            Q54=makeQuery(id+"F0.imprint","IMPRINT",FACE,{"disambiguationData":[TD([[makeQuery(id+"F0.imprint","IMPRINT",EDGE,{"derivedFrom":sQuery(id+"F0.wireOp",EDGE,"E56.bottom")}),-1.0]])]});
            var Q55;
            Q55=makeQuery(id+"F0.imprint","IMPRINT",FACE,{"disambiguationData":[TD([[makeQuery(id+"F0.imprint","IMPRINT",EDGE,{"derivedFrom":sQuery(id+"F0.wireOp",EDGE,"E58.bottom")}),1.0]])]});
            var Q56;
            Q56=makeQuery(id+"F0.imprint","IMPRINT",FACE,{"disambiguationData":[TD([[makeQuery(id+"F0.imprint","IMPRINT",EDGE,{"derivedFrom":sQuery(id+"F0.wireOp",EDGE,"E49.bottom")}),1.0]])]});
            var Q57;
            Q57=makeQuery(id+"F0.imprint","IMPRINT",FACE,{"disambiguationData":[TD([[makeQuery(id+"F0.imprint","IMPRINT",EDGE,{"derivedFrom":sQuery(id+"F0.wireOp",EDGE,"E51.bottom")}),-1.0]])]});
            var Q58;
            Q58=makeQuery(id+"F0.imprint","IMPRINT",FACE,{"disambiguationData":[TD([[makeQuery(id+"F0.imprint","IMPRINT",EDGE,{"derivedFrom":sQuery(id+"F0.wireOp",EDGE,"E27.top")}),-1.0]])]});
            var Q59;
            Q59=makeQuery(id+"F0.imprint","IMPRINT",FACE,{"disambiguationData":[TD([[makeQuery(id+"F0.imprint","IMPRINT",EDGE,{"derivedFrom":sQuery(id+"F0.wireOp",EDGE,"E52.bottom")}),-1.0]])]});
            var Q60;
            Q60=makeQuery(id+"F0.imprint","IMPRINT",FACE,{"disambiguationData":[TD([[makeQuery(id+"F0.imprint","IMPRINT",EDGE,{"derivedFrom":sQuery(id+"F0.wireOp",EDGE,"E59.bottom")}),1.0]])]});
            var Q61;
            Q61=makeQuery(id+"F0.imprint","IMPRINT",FACE,{"disambiguationData":[TD([[makeQuery(id+"F0.imprint","IMPRINT",EDGE,{"derivedFrom":sQuery(id+"F0.wireOp",EDGE,"E47.top")}),1.0]])]});
            var Q62;
            Q62=makeQuery(id+"F0.imprint","IMPRINT",FACE,{"disambiguationData":[TD([[makeQuery(id+"F0.imprint","IMPRINT",EDGE,{"derivedFrom":sQuery(id+"F0.wireOp",EDGE,"E37.bottom")}),-1.0]])]});
            var Q63;
            Q63=makeQuery(id+"F0.imprint","IMPRINT",FACE,{"disambiguationData":[TD([[makeQuery(id+"F0.imprint","IMPRINT",EDGE,{"derivedFrom":sQuery(id+"F0.wireOp",EDGE,"E35.bottom")}),-1.0]])]});
            var Q64;
            Q64=makeQuery(id+"F0.imprint","IMPRINT",FACE,{"disambiguationData":[TD([[makeQuery(id+"F0.imprint","IMPRINT",EDGE,{"derivedFrom":sQuery(id+"F0.wireOp",EDGE,"E23.bottom")}),1.0]])]});
            var Q65;
            Q65=makeQuery(id+"F0.imprint","IMPRINT",FACE,{"disambiguationData":[TD([[makeQuery(id+"F0.imprint","IMPRINT",EDGE,{"derivedFrom":sQuery(id+"F0.wireOp",EDGE,"E24.bottom")}),1.0]])]});
            var Q66;
            Q66=makeQuery(id+"F0.imprint","IMPRINT",FACE,{"disambiguationData":[TD([[makeQuery(id+"F0.imprint","IMPRINT",EDGE,{"derivedFrom":sQuery(id+"F0.wireOp",EDGE,"E31.bottom")}),1.0]])]});
            var Q67;
            Q67=makeQuery(id+"F0.imprint","IMPRINT",FACE,{"disambiguationData":[TD([[makeQuery(id+"F0.imprint","IMPRINT",EDGE,{"derivedFrom":sQuery(id+"F0.wireOp",EDGE,"E39.bottom")}),1.0]])]});
            extrude(context, id + "F1", {"entities" : qUnion([Q0, Q1, Q2, Q3, Q4, Q5, Q6, Q7, Q8, Q9, Q10, Q11, Q12, Q13, Q14, Q15, Q16, Q17, Q18, Q19, Q20, Q21, Q22, Q23, Q24, Q25, Q26, Q27, Q28, Q29, Q30, Q31, Q32, Q33, Q34, Q35, Q36, Q37, Q38, Q39, Q40, Q41, Q42, Q43, Q44, Q45, Q46, Q47, Q48, Q49, Q50, Q51, Q52, Q53, Q54, Q55, Q56, Q57, Q58, Q59, Q60, Q61, Q62, Q63, Q64, Q65, Q66, Q67]), "depth" : 5.08 * mm, "offsetDistance" : 25.4 * mm});
        }
        {
            var Q0;
            Q0=qCreatedBy(makeId("Top.planeOp"),FACE);
            var sketch = newSketch(context, id + "F2", { "sketchPlane" : qUnion([Q0])});
            skLineSegment(sketch, "E64.bottom", {"start": v(-10.13, 43.09) * mm, "end": v(2.45, 43.09) * mm});
            skLineSegment(sketch, "E64.top", {"start": v(-10.13, 26.42) * mm, "end": v(2.45, 26.42) * mm});
            skLineSegment(sketch, "E64.left", {"start": v(-10.13, 43.09) * mm, "end": v(-10.13, 26.42) * mm});
            skLineSegment(sketch, "E64.right", {"start": v(2.45, 43.09) * mm, "end": v(2.45, 26.42) * mm});
            skLineSegment(sketch, "E65.bottom", {"start": v(2.45, 26.42) * mm, "end": v(6.64, 26.42) * mm});
            skLineSegment(sketch, "E65.top", {"start": v(2.45, 38.64) * mm, "end": v(6.64, 38.64) * mm});
            skLineSegment(sketch, "E65.left", {"start": v(2.45, 26.42) * mm, "end": v(2.45, 38.64) * mm});
            skLineSegment(sketch, "E65.right", {"start": v(6.64, 26.42) * mm, "end": v(6.64, 38.64) * mm});
            skLineSegment(sketch, "E66.bottom", {"start": v(6.64, 26.42) * mm, "end": v(10.77, 26.42) * mm});
            skLineSegment(sketch, "E66.top", {"start": v(6.64, 30.38) * mm, "end": v(10.77, 30.38) * mm});
            skLineSegment(sketch, "E66.left", {"start": v(6.64, 26.42) * mm, "end": v(6.64, 30.38) * mm});
            skLineSegment(sketch, "E66.right", {"start": v(10.77, 26.42) * mm, "end": v(10.77, 30.38) * mm});
            skLineSegment(sketch, "E67.bottom", {"start": v(10.77, 26.42) * mm, "end": v(19.1, 26.42) * mm});
            skLineSegment(sketch, "E67.top", {"start": v(10.77, 22.19) * mm, "end": v(19.1, 22.19) * mm});
            skLineSegment(sketch, "E67.left", {"start": v(10.77, 26.42) * mm, "end": v(10.77, 22.19) * mm});
            skLineSegment(sketch, "E67.right", {"start": v(19.1, 26.42) * mm, "end": v(19.1, 22.19) * mm});
            skLineSegment(sketch, "E68.bottom", {"start": v(19.1, 26.42) * mm, "end": v(23.38, 26.42) * mm});
            skLineSegment(sketch, "E68.top", {"start": v(19.1, 34.84) * mm, "end": v(23.38, 34.84) * mm});
            skLineSegment(sketch, "E68.left", {"start": v(19.1, 26.42) * mm, "end": v(19.1, 34.84) * mm});
            skLineSegment(sketch, "E68.right", {"start": v(23.38, 26.42) * mm, "end": v(23.38, 34.84) * mm});
            skLineSegment(sketch, "E69.bottom", {"start": v(-10.13, 38.78) * mm, "end": v(-14.28, 38.78) * mm});
            skLineSegment(sketch, "E69.top", {"start": v(-10.13, 9.64) * mm, "end": v(-14.28, 9.64) * mm});
            skLineSegment(sketch, "E69.left", {"start": v(-10.13, 38.78) * mm, "end": v(-10.13, 9.64) * mm});
            skLineSegment(sketch, "E69.right", {"start": v(-14.28, 38.78) * mm, "end": v(-14.28, 9.64) * mm});
            skLineSegment(sketch, "E70.bottom", {"start": v(-10.13, 26.42) * mm, "end": v(-5.94, 26.42) * mm});
            skLineSegment(sketch, "E70.top", {"start": v(-10.13, 22.19) * mm, "end": v(-5.94, 22.19) * mm});
            skLineSegment(sketch, "E70.left", {"start": v(-10.13, 26.42) * mm, "end": v(-10.13, 22.19) * mm});
            skLineSegment(sketch, "E70.right", {"start": v(-5.94, 26.42) * mm, "end": v(-5.94, 22.19) * mm});
            skLineSegment(sketch, "E71.bottom", {"start": v(-10.13, 9.64) * mm, "end": v(-5.96, 9.64) * mm});
            skLineSegment(sketch, "E71.top", {"start": v(-10.13, 5.28) * mm, "end": v(-5.96, 5.28) * mm});
            skLineSegment(sketch, "E71.left", {"start": v(-10.13, 9.64) * mm, "end": v(-10.13, 5.28) * mm});
            skLineSegment(sketch, "E71.right", {"start": v(-5.96, 9.64) * mm, "end": v(-5.96, 5.28) * mm});
            skLineSegment(sketch, "E72.bottom", {"start": v(52.8, 9.64) * mm, "end": v(40.16, 9.64) * mm});
            skLineSegment(sketch, "E72.top", {"start": v(52.8, 13.6) * mm, "end": v(40.16, 13.6) * mm});
            skLineSegment(sketch, "E72.left", {"start": v(52.8, 9.64) * mm, "end": v(52.8, 13.6) * mm});
            skLineSegment(sketch, "E72.right", {"start": v(40.16, 9.64) * mm, "end": v(40.16, 13.6) * mm});
            skLineSegment(sketch, "E73.bottom", {"start": v(40.16, 9.64) * mm, "end": v(44.27, 9.64) * mm});
            skLineSegment(sketch, "E73.top", {"start": v(40.16, -3.1) * mm, "end": v(44.27, -3.1) * mm});
            skLineSegment(sketch, "E73.left", {"start": v(40.16, 9.64) * mm, "end": v(40.16, -3.1) * mm});
            skLineSegment(sketch, "E73.right", {"start": v(44.27, 9.64) * mm, "end": v(44.27, -3.1) * mm});
            skLineSegment(sketch, "E74.bottom", {"start": v(44.27, -3.1) * mm, "end": v(52.74, -3.1) * mm});
            skLineSegment(sketch, "E74.top", {"start": v(44.27, 5.25) * mm, "end": v(52.74, 5.25) * mm});
            skLineSegment(sketch, "E74.left", {"start": v(44.27, -3.1) * mm, "end": v(44.27, 5.25) * mm});
            skLineSegment(sketch, "E74.right", {"start": v(52.74, -3.1) * mm, "end": v(52.74, 5.25) * mm});
            skLineSegment(sketch, "E75.bottom", {"start": v(52.74, 5.25) * mm, "end": v(56.88, 5.25) * mm});
            skLineSegment(sketch, "E75.top", {"start": v(52.74, 1.06) * mm, "end": v(56.88, 1.06) * mm});
            skLineSegment(sketch, "E75.left", {"start": v(52.74, 5.25) * mm, "end": v(52.74, 1.06) * mm});
            skLineSegment(sketch, "E75.right", {"start": v(56.88, 5.25) * mm, "end": v(56.88, 1.06) * mm});
            skLineSegment(sketch, "E76.bottom", {"start": v(65.5, 1.07) * mm, "end": v(61.15, 1.07) * mm});
            skLineSegment(sketch, "E76.top", {"start": v(65.5, 5.25) * mm, "end": v(61.15, 5.25) * mm});
            skLineSegment(sketch, "E76.left", {"start": v(65.5, 1.07) * mm, "end": v(65.5, 5.25) * mm});
            skLineSegment(sketch, "E76.right", {"start": v(61.15, 1.07) * mm, "end": v(61.15, 5.25) * mm});
            skLineSegment(sketch, "E77.bottom", {"start": v(-43.78, 13.67) * mm, "end": v(-39.5, 13.67) * mm});
            skLineSegment(sketch, "E77.top", {"start": v(-43.78, 1.1) * mm, "end": v(-39.5, 1.1) * mm});
            skLineSegment(sketch, "E77.left", {"start": v(-43.78, 13.67) * mm, "end": v(-43.78, 1.1) * mm});
            skLineSegment(sketch, "E77.right", {"start": v(-39.5, 13.67) * mm, "end": v(-39.5, 1.1) * mm});
            skLineSegment(sketch, "E78.bottom", {"start": v(-39.5, 9.64) * mm, "end": v(-31.17, 9.64) * mm});
            skLineSegment(sketch, "E78.top", {"start": v(-39.5, -3.1) * mm, "end": v(-31.17, -3.1) * mm});
            skLineSegment(sketch, "E78.left", {"start": v(-39.5, 9.64) * mm, "end": v(-39.5, -3.1) * mm});
            skLineSegment(sketch, "E78.right", {"start": v(-31.17, 9.64) * mm, "end": v(-31.17, -3.1) * mm});
            skLineSegment(sketch, "E79.bottom", {"start": v(-35.33, -3.1) * mm, "end": v(-18.75, -3.1) * mm});
            skLineSegment(sketch, "E79.top", {"start": v(-35.33, -7.18) * mm, "end": v(-18.75, -7.18) * mm});
            skLineSegment(sketch, "E79.left", {"start": v(-35.33, -3.1) * mm, "end": v(-35.33, -7.18) * mm});
            skLineSegment(sketch, "E79.right", {"start": v(-18.75, -3.1) * mm, "end": v(-18.75, -7.18) * mm});
            skLineSegment(sketch, "E80.bottom", {"start": v(-31.14, -7.18) * mm, "end": v(-22.85, -7.18) * mm});
            skLineSegment(sketch, "E80.top", {"start": v(-31.14, -11.48) * mm, "end": v(-22.85, -11.48) * mm});
            skLineSegment(sketch, "E80.left", {"start": v(-31.14, -7.18) * mm, "end": v(-31.14, -11.48) * mm});
            skLineSegment(sketch, "E80.right", {"start": v(-22.85, -7.18) * mm, "end": v(-22.85, -11.48) * mm});
            skLineSegment(sketch, "E81.bottom", {"start": v(-18.75, -3.1) * mm, "end": v(-26.9, -3.1) * mm});
            skLineSegment(sketch, "E81.top", {"start": v(-18.75, 1.13) * mm, "end": v(-26.9, 1.13) * mm});
            skLineSegment(sketch, "E81.left", {"start": v(-18.75, -3.1) * mm, "end": v(-18.75, 1.13) * mm});
            skLineSegment(sketch, "E81.right", {"start": v(-26.9, -3.1) * mm, "end": v(-26.9, 1.13) * mm});
            skLineSegment(sketch, "E82.bottom", {"start": v(-26.9, 1.13) * mm, "end": v(-22.9, 1.13) * mm});
            skLineSegment(sketch, "E82.top", {"start": v(-26.9, 5.34) * mm, "end": v(-22.9, 5.34) * mm});
            skLineSegment(sketch, "E82.left", {"start": v(-26.9, 1.13) * mm, "end": v(-26.9, 5.34) * mm});
            skLineSegment(sketch, "E82.right", {"start": v(-22.9, 1.13) * mm, "end": v(-22.9, 5.34) * mm});
            skLineSegment(sketch, "E83.bottom", {"start": v(-22.85, -11.48) * mm, "end": v(-14.34, -11.48) * mm});
            skLineSegment(sketch, "E83.top", {"start": v(-22.85, -24.12) * mm, "end": v(-14.34, -24.12) * mm});
            skLineSegment(sketch, "E83.left", {"start": v(-22.85, -11.48) * mm, "end": v(-22.85, -24.12) * mm});
            skLineSegment(sketch, "E83.right", {"start": v(-14.34, -11.48) * mm, "end": v(-14.34, -24.12) * mm});
            skLineSegment(sketch, "E84.bottom", {"start": v(-14.34, -24.12) * mm, "end": v(2.37, -24.12) * mm});
            skLineSegment(sketch, "E84.top", {"start": v(-14.34, -15.57) * mm, "end": v(2.37, -15.57) * mm});
            skLineSegment(sketch, "E84.left", {"start": v(-14.34, -24.12) * mm, "end": v(-14.34, -15.57) * mm});
            skLineSegment(sketch, "E84.right", {"start": v(2.37, -24.12) * mm, "end": v(2.37, -15.57) * mm});
            skLineSegment(sketch, "E85.bottom", {"start": v(2.37, -15.57) * mm, "end": v(6.61, -15.57) * mm});
            skLineSegment(sketch, "E85.top", {"start": v(2.37, -19.85) * mm, "end": v(6.61, -19.85) * mm});
            skLineSegment(sketch, "E85.left", {"start": v(2.37, -15.57) * mm, "end": v(2.37, -19.85) * mm});
            skLineSegment(sketch, "E85.right", {"start": v(6.61, -15.57) * mm, "end": v(6.61, -19.85) * mm});
            skLineSegment(sketch, "E86.bottom", {"start": v(-18.6, -24.12) * mm, "end": v(-1.8, -24.12) * mm});
            skLineSegment(sketch, "E86.top", {"start": v(-18.6, -28.16) * mm, "end": v(-1.8, -28.16) * mm});
            skLineSegment(sketch, "E86.left", {"start": v(-18.6, -24.12) * mm, "end": v(-18.6, -28.16) * mm});
            skLineSegment(sketch, "E86.right", {"start": v(-1.8, -24.12) * mm, "end": v(-1.8, -28.16) * mm});
            skLineSegment(sketch, "E87.bottom", {"start": v(-26.9, -45.01) * mm, "end": v(-39.61, -45.01) * mm});
            skLineSegment(sketch, "E87.top", {"start": v(-26.9, -32.36) * mm, "end": v(-39.61, -32.36) * mm});
            skLineSegment(sketch, "E87.left", {"start": v(-26.9, -45.01) * mm, "end": v(-26.9, -32.36) * mm});
            skLineSegment(sketch, "E87.right", {"start": v(-39.61, -45.01) * mm, "end": v(-39.61, -32.36) * mm});
            skLineSegment(sketch, "E88.bottom", {"start": v(-26.9, -40.8) * mm, "end": v(-22.85, -40.8) * mm});
            skLineSegment(sketch, "E88.top", {"start": v(-26.9, -36.72) * mm, "end": v(-22.85, -36.72) * mm});
            skLineSegment(sketch, "E88.left", {"start": v(-26.9, -40.8) * mm, "end": v(-26.9, -36.72) * mm});
            skLineSegment(sketch, "E88.right", {"start": v(-22.85, -40.8) * mm, "end": v(-22.85, -36.72) * mm});
            skLineSegment(sketch, "E89.bottom", {"start": v(-31.18, -32.36) * mm, "end": v(-35.36, -32.36) * mm});
            skLineSegment(sketch, "E89.top", {"start": v(-31.18, -28.16) * mm, "end": v(-35.36, -28.16) * mm});
            skLineSegment(sketch, "E89.left", {"start": v(-31.18, -32.36) * mm, "end": v(-31.18, -28.16) * mm});
            skLineSegment(sketch, "E89.right", {"start": v(-35.36, -32.36) * mm, "end": v(-35.36, -28.16) * mm});
            skLineSegment(sketch, "E90.bottom", {"start": v(-39.61, -45.01) * mm, "end": v(-47.92, -45.01) * mm});
            skLineSegment(sketch, "E90.top", {"start": v(-39.61, -36.67) * mm, "end": v(-47.92, -36.67) * mm});
            skLineSegment(sketch, "E90.left", {"start": v(-39.61, -45.01) * mm, "end": v(-39.61, -36.67) * mm});
            skLineSegment(sketch, "E90.right", {"start": v(-47.92, -45.01) * mm, "end": v(-47.92, -36.67) * mm});
            skLineSegment(sketch, "E91.bottom", {"start": v(-47.92, -45.01) * mm, "end": v(-56.43, -45.01) * mm});
            skLineSegment(sketch, "E91.top", {"start": v(-47.92, -40.95) * mm, "end": v(-56.43, -40.95) * mm});
            skLineSegment(sketch, "E91.left", {"start": v(-47.92, -45.01) * mm, "end": v(-47.92, -40.95) * mm});
            skLineSegment(sketch, "E91.right", {"start": v(-56.43, -45.01) * mm, "end": v(-56.43, -40.95) * mm});
            skLineSegment(sketch, "E92.bottom", {"start": v(23.33, -45.01) * mm, "end": v(-5.84, -45.01) * mm});
            skLineSegment(sketch, "E92.top", {"start": v(23.33, -40.91) * mm, "end": v(-5.84, -40.91) * mm});
            skLineSegment(sketch, "E92.left", {"start": v(23.33, -45.01) * mm, "end": v(23.33, -40.91) * mm});
            skLineSegment(sketch, "E92.right", {"start": v(-5.84, -45.01) * mm, "end": v(-5.84, -40.91) * mm});
            skLineSegment(sketch, "E93.bottom", {"start": v(-1.8, -40.91) * mm, "end": v(10.72, -40.91) * mm});
            skLineSegment(sketch, "E93.top", {"start": v(-1.8, -32.4) * mm, "end": v(10.72, -32.4) * mm});
            skLineSegment(sketch, "E93.left", {"start": v(-1.8, -40.91) * mm, "end": v(-1.8, -32.4) * mm});
            skLineSegment(sketch, "E93.right", {"start": v(10.72, -40.91) * mm, "end": v(10.72, -32.4) * mm});
            skLineSegment(sketch, "E94.bottom", {"start": v(10.72, -32.4) * mm, "end": v(6.6, -32.4) * mm});
            skLineSegment(sketch, "E94.top", {"start": v(10.72, -28.16) * mm, "end": v(6.6, -28.16) * mm});
            skLineSegment(sketch, "E94.left", {"start": v(10.72, -32.4) * mm, "end": v(10.72, -28.16) * mm});
            skLineSegment(sketch, "E94.right", {"start": v(6.6, -32.4) * mm, "end": v(6.6, -28.16) * mm});
            skLineSegment(sketch, "E95.bottom", {"start": v(10.72, -28.16) * mm, "end": v(14.91, -28.16) * mm});
            skLineSegment(sketch, "E95.top", {"start": v(10.72, -36.76) * mm, "end": v(14.91, -36.76) * mm});
            skLineSegment(sketch, "E95.left", {"start": v(10.72, -28.16) * mm, "end": v(10.72, -36.76) * mm});
            skLineSegment(sketch, "E95.right", {"start": v(14.91, -28.16) * mm, "end": v(14.91, -36.76) * mm});
            skSolve(sketch);
        }
        {
            var Q0;
            {var subQ0=sQuery(id+"F2.wireOp",EDGE,"E93.left");var subQ4=sQuery(id+"F2.wireOp",EDGE,"E94.left");var subQ15=makeQuery(id+"F2.imprint","IMPRINT",EDGE,{"derivedFrom":subQ4});var subQ28=sQuery(id+"F2.wireOp",EDGE,"E87.bottom");var subQ31=sQuery(id+"F2.wireOp",EDGE,"E88.bottom");var subQ34=sQuery(id+"F2.wireOp",EDGE,"E90.bottom");var subQ41=sQuery(id+"F2.wireOp",EDGE,"E91.bottom");var subQ43=sQuery(id+"F2.wireOp",EDGE,"E84.top");var subQ55=sQuery(id+"F2.wireOp",EDGE,"E85.bottom");var subQ65=sQuery(id+"F2.wireOp",EDGE,"E81.left");var subQ74=sQuery(id+"F2.wireOp",EDGE,"E79.left");var subQ81=sQuery(id+"F2.wireOp",EDGE,"E83.bottom");var subQ88=sQuery(id+"F2.wireOp",EDGE,"E78.bottom");var subQ93=sQuery(id+"F2.wireOp",EDGE,"E77.bottom");var subQ94=sQuery(id+"F2.wireOp",EDGE,"E75.bottom");var subQ100=sQuery(id+"F2.wireOp",EDGE,"E74.bottom");var subQ102=sQuery(id+"F2.wireOp",EDGE,"E73.top");var subQ111=sQuery(id+"F2.wireOp",EDGE,"E69.bottom");var subQ121=sQuery(id+"F2.wireOp",EDGE,"E65.bottom");var subQ124=sQuery(id+"F2.wireOp",EDGE,"E64.bottom");var subQ129=sQuery(id+"F2.wireOp",EDGE,"E71.bottom");var subQ131=sQuery(id+"F2.wireOp",EDGE,"E70.top");var subQ137=sQuery(id+"F2.wireOp",EDGE,"E66.bottom");Q0=qUnion([makeQuery(id+"F2.imprint","IMPRINT",FACE,{"disambiguationData":[TD([[makeQuery(id+"F2.imprint","IMPRINT",EDGE,{"derivedFrom":sQuery(id+"F2.wireOp",EDGE,"E67.bottom")}),-1.0]])]}),makeQuery(id+"F2.imprint","IMPRINT",FACE,{"disambiguationData":[TD([[makeQuery(id+"F2.imprint","IMPRINT",EDGE,{"derivedFrom":subQ137}),1.0]])]}),makeQuery(id+"F2.imprint","IMPRINT",FACE,{"disambiguationData":[TD([[makeQuery(id+"F2.imprint","IMPRINT",EDGE,{"derivedFrom":sQuery(id+"F2.wireOp",EDGE,"E68.bottom")}),1.0]])]}),makeQuery(id+"F2.imprint","IMPRINT",FACE,{"disambiguationData":[TD([[makeQuery(id+"F2.imprint","IMPRINT",EDGE,{"derivedFrom":subQ121}),1.0]])]}),makeQuery(id+"F2.imprint","IMPRINT",FACE,{"disambiguationData":[TD([[makeQuery(id+"F2.imprint","IMPRINT",EDGE,{"derivedFrom":subQ129}),-1.0]])]}),makeQuery(id+"F2.imprint","IMPRINT",FACE,{"disambiguationData":[TD([[makeQuery(id+"F2.imprint","IMPRINT",EDGE,{"derivedFrom":subQ131}),1.0]])]}),makeQuery(id+"F2.imprint","IMPRINT",FACE,{"disambiguationData":[TD([[makeQuery(id+"F2.imprint","IMPRINT",EDGE,{"derivedFrom":subQ111}),1.0]])]}),makeQuery(id+"F2.imprint","IMPRINT",FACE,{"disambiguationData":[TD([[makeQuery(id+"F2.imprint","IMPRINT",EDGE,{"derivedFrom":subQ124}),-1.0]])]}),makeQuery(id+"F2.imprint","IMPRINT",FACE,{"disambiguationData":[TD([[makeQuery(id+"F2.imprint","IMPRINT",EDGE,{"derivedFrom":sQuery(id+"F2.wireOp",EDGE,"E76.bottom")}),-1.0]])]}),makeQuery(id+"F2.imprint","IMPRINT",FACE,{"disambiguationData":[TD([[makeQuery(id+"F2.imprint","IMPRINT",EDGE,{"derivedFrom":sQuery(id+"F2.wireOp",EDGE,"E72.top")}),1.0]])]}),makeQuery(id+"F2.imprint","IMPRINT",FACE,{"disambiguationData":[TD([[makeQuery(id+"F2.imprint","IMPRINT",EDGE,{"derivedFrom":subQ94}),-1.0]])]}),makeQuery(id+"F2.imprint","IMPRINT",FACE,{"disambiguationData":[TD([[makeQuery(id+"F2.imprint","IMPRINT",EDGE,{"derivedFrom":subQ102}),1.0]])]}),makeQuery(id+"F2.imprint","IMPRINT",FACE,{"disambiguationData":[TD([[makeQuery(id+"F2.imprint","IMPRINT",EDGE,{"derivedFrom":subQ100}),1.0]])]}),makeQuery(id+"F2.imprint","IMPRINT",FACE,{"disambiguationData":[TD([[makeQuery(id+"F2.imprint","IMPRINT",EDGE,{"derivedFrom":subQ93}),-1.0]])]}),makeQuery(id+"F2.imprint","IMPRINT",FACE,{"disambiguationData":[TD([[makeQuery(id+"F2.imprint","IMPRINT",EDGE,{"derivedFrom":sQuery(id+"F2.wireOp",EDGE,"E80.top")}),1.0]])]}),makeQuery(id+"F2.imprint","IMPRINT",FACE,{"disambiguationData":[TD([[makeQuery(id+"F2.imprint","IMPRINT",EDGE,{"derivedFrom":sQuery(id+"F2.wireOp",EDGE,"E82.top")}),-1.0]])]}),makeQuery(id+"F2.imprint","IMPRINT",FACE,{"disambiguationData":[TD([[makeQuery(id+"F2.imprint","IMPRINT",EDGE,{"derivedFrom":subQ55}),-1.0]])]}),makeQuery(id+"F2.imprint","IMPRINT",FACE,{"disambiguationData":[TD([[makeQuery(id+"F2.imprint","IMPRINT",EDGE,{"derivedFrom":subQ88}),-1.0]])]}),makeQuery(id+"F2.imprint","IMPRINT",FACE,{"disambiguationData":[TD([[makeQuery(id+"F2.imprint","IMPRINT",EDGE,{"derivedFrom":subQ65}),1.0]])]}),makeQuery(id+"F2.imprint","IMPRINT",FACE,{"disambiguationData":[TD([[makeQuery(id+"F2.imprint","IMPRINT",EDGE,{"derivedFrom":subQ81}),-1.0]])]}),makeQuery(id+"F2.imprint","IMPRINT",FACE,{"disambiguationData":[TD([[makeQuery(id+"F2.imprint","IMPRINT",EDGE,{"derivedFrom":sQuery(id+"F2.wireOp",EDGE,"E86.top")}),1.0]])]}),makeQuery(id+"F2.imprint","IMPRINT",FACE,{"disambiguationData":[TD([[makeQuery(id+"F2.imprint","IMPRINT",EDGE,{"derivedFrom":subQ74}),1.0]])]}),makeQuery(id+"F2.imprint","IMPRINT",FACE,{"disambiguationData":[TD([[makeQuery(id+"F2.imprint","IMPRINT",EDGE,{"derivedFrom":subQ43}),-1.0]])]}),makeQuery(id+"F2.imprint","IMPRINT",FACE,{"disambiguationData":[TD([[makeQuery(id+"F2.imprint","IMPRINT",EDGE,{"derivedFrom":subQ41}),-1.0]])]}),makeQuery(id+"F2.imprint","IMPRINT",FACE,{"disambiguationData":[TD([[makeQuery(id+"F2.imprint","IMPRINT",EDGE,{"derivedFrom":sQuery(id+"F2.wireOp",EDGE,"E89.top")}),1.0]])]}),makeQuery(id+"F2.imprint","IMPRINT",FACE,{"disambiguationData":[TD([[makeQuery(id+"F2.imprint","IMPRINT",EDGE,{"derivedFrom":subQ31}),1.0]])]}),makeQuery(id+"F2.imprint","IMPRINT",FACE,{"disambiguationData":[TD([[makeQuery(id+"F2.imprint","IMPRINT",EDGE,{"derivedFrom":subQ34}),-1.0]])]}),makeQuery(id+"F2.imprint","IMPRINT",FACE,{"disambiguationData":[TD([[makeQuery(id+"F2.imprint","IMPRINT",EDGE,{"derivedFrom":subQ28}),-1.0]])]}),makeQuery(id+"F2.imprint","IMPRINT",FACE,{"disambiguationData":[TD([[makeQuery(id+"F2.imprint","IMPRINT",EDGE,{"derivedFrom":sQuery(id+"F2.wireOp",EDGE,"E92.bottom")}),-1.0]])]}),makeQuery(id+"F2.imprint","IMPRINT",FACE,{"disambiguationData":[TD([[makeQuery(id+"F2.imprint","IMPRINT",EDGE,{"derivedFrom":sQuery(id+"F2.wireOp",EDGE,"E94.top")}),1.0]])]}),makeQuery(id+"F2.imprint","IMPRINT",FACE,{"disambiguationData":[TD([[subQ15,-1.0]])]}),makeQuery(id+"F2.imprint","IMPRINT",FACE,{"disambiguationData":[TD([[makeQuery(id+"F2.imprint","IMPRINT",EDGE,{"derivedFrom":subQ0}),-1.0]])]})]);}
            extrude(context, id + "F3", {"entities" : qUnion([Q0]), "depth" : 3.8 * mm, "offsetDistance" : 25.4 * mm});
        }
        {
            var Q0;
            Q0=qCreatedBy(makeId("Top.planeOp"),FACE);
            var sketch = newSketch(context, id + "F4", { "sketchPlane" : qUnion([Q0])});
            skLineSegment(sketch, "E96.bottom", {"start": v(23.37, 9.55) * mm, "end": v(19.18, 9.55) * mm});
            skLineSegment(sketch, "E96.top", {"start": v(23.37, 13.59) * mm, "end": v(19.18, 13.59) * mm});
            skLineSegment(sketch, "E96.left", {"start": v(23.37, 9.55) * mm, "end": v(23.37, 13.59) * mm});
            skLineSegment(sketch, "E96.right", {"start": v(19.18, 9.55) * mm, "end": v(19.18, 13.59) * mm});
            skLineSegment(sketch, "E97.bottom", {"start": v(19.18, 9.55) * mm, "end": v(14.92, 9.55) * mm});
            skLineSegment(sketch, "E97.top", {"start": v(19.18, 5.23) * mm, "end": v(14.92, 5.23) * mm});
            skLineSegment(sketch, "E97.left", {"start": v(19.18, 9.55) * mm, "end": v(19.18, 5.23) * mm});
            skLineSegment(sketch, "E97.right", {"start": v(14.92, 9.55) * mm, "end": v(14.92, 5.23) * mm});
            skLineSegment(sketch, "E98.bottom", {"start": v(14.92, 9.55) * mm, "end": v(10.78, 9.55) * mm});
            skLineSegment(sketch, "E98.top", {"start": v(14.92, 22.16) * mm, "end": v(10.78, 22.16) * mm});
            skLineSegment(sketch, "E98.left", {"start": v(14.92, 9.55) * mm, "end": v(14.92, 22.16) * mm});
            skLineSegment(sketch, "E98.right", {"start": v(10.78, 9.55) * mm, "end": v(10.78, 22.16) * mm});
            skLineSegment(sketch, "E99.bottom", {"start": v(14.92, 5.23) * mm, "end": v(-5.9, 5.23) * mm});
            skLineSegment(sketch, "E99.top", {"start": v(14.92, 0.92) * mm, "end": v(-5.9, 0.92) * mm});
            skLineSegment(sketch, "E99.left", {"start": v(14.92, 5.23) * mm, "end": v(14.92, 0.92) * mm});
            skLineSegment(sketch, "E99.right", {"start": v(-5.9, 5.23) * mm, "end": v(-5.9, 0.92) * mm});
            skLineSegment(sketch, "E100.bottom", {"start": v(-1.85, 5.23) * mm, "end": v(-5.9, 5.23) * mm});
            skLineSegment(sketch, "E100.top", {"start": v(-1.85, 13.62) * mm, "end": v(-5.9, 13.62) * mm});
            skLineSegment(sketch, "E100.left", {"start": v(-1.85, 5.23) * mm, "end": v(-1.85, 13.62) * mm});
            skLineSegment(sketch, "E100.right", {"start": v(-5.9, 5.23) * mm, "end": v(-5.9, 13.62) * mm});
            skLineSegment(sketch, "E101.bottom", {"start": v(-5.9, 9.55) * mm, "end": v(-10.16, 9.55) * mm});
            skLineSegment(sketch, "E101.top", {"start": v(-5.9, 22.19) * mm, "end": v(-10.16, 22.19) * mm});
            skLineSegment(sketch, "E101.left", {"start": v(-5.9, 9.55) * mm, "end": v(-5.9, 22.19) * mm});
            skLineSegment(sketch, "E101.right", {"start": v(-10.16, 9.55) * mm, "end": v(-10.16, 22.19) * mm});
            skLineSegment(sketch, "E102.bottom", {"start": v(-5.9, 22.19) * mm, "end": v(-1.75, 22.19) * mm});
            skLineSegment(sketch, "E102.top", {"start": v(-5.9, 26.4) * mm, "end": v(-1.75, 26.4) * mm});
            skLineSegment(sketch, "E102.left", {"start": v(-5.9, 22.19) * mm, "end": v(-5.9, 26.4) * mm});
            skLineSegment(sketch, "E102.right", {"start": v(-1.75, 22.19) * mm, "end": v(-1.75, 26.4) * mm});
            skSolve(sketch);
        }
        {
            var Q0;
            Q0=qCreatedBy(makeId("Top.planeOp"),FACE);
            var sketch = newSketch(context, id + "F5", { "sketchPlane" : qUnion([Q0])});
            skLineSegment(sketch, "E103.bottom", {"start": v(19.2, 9.56) * mm, "end": v(14.81, 9.56) * mm});
            skLineSegment(sketch, "E103.top", {"start": v(19.2, 13.57) * mm, "end": v(14.81, 13.57) * mm});
            skLineSegment(sketch, "E103.left", {"start": v(19.2, 9.56) * mm, "end": v(19.2, 13.57) * mm});
            skLineSegment(sketch, "E103.right", {"start": v(14.81, 9.56) * mm, "end": v(14.81, 13.57) * mm});
            skLineSegment(sketch, "E104.bottom", {"start": v(19.2, 13.57) * mm, "end": v(23.4, 13.57) * mm});
            skLineSegment(sketch, "E104.top", {"start": v(19.2, 26.43) * mm, "end": v(23.4, 26.43) * mm});
            skLineSegment(sketch, "E104.left", {"start": v(19.2, 13.57) * mm, "end": v(19.2, 26.43) * mm});
            skLineSegment(sketch, "E104.right", {"start": v(23.4, 13.57) * mm, "end": v(23.4, 26.43) * mm});
            skLineSegment(sketch, "E105.bottom", {"start": v(10.73, 9.61) * mm, "end": v(-1.85, 9.61) * mm});
            skLineSegment(sketch, "E105.top", {"start": v(10.73, 13.57) * mm, "end": v(-1.85, 13.57) * mm});
            skLineSegment(sketch, "E105.left", {"start": v(10.73, 9.61) * mm, "end": v(10.73, 13.57) * mm});
            skLineSegment(sketch, "E105.right", {"start": v(-1.85, 9.61) * mm, "end": v(-1.85, 13.57) * mm});
            skLineSegment(sketch, "E106.bottom", {"start": v(2.35, 13.57) * mm, "end": v(-5.9, 13.57) * mm});
            skLineSegment(sketch, "E106.top", {"start": v(2.35, 22.21) * mm, "end": v(-5.9, 22.21) * mm});
            skLineSegment(sketch, "E106.left", {"start": v(2.35, 13.57) * mm, "end": v(2.35, 22.21) * mm});
            skLineSegment(sketch, "E106.right", {"start": v(-5.9, 13.57) * mm, "end": v(-5.9, 22.21) * mm});
            skLineSegment(sketch, "E107.bottom", {"start": v(-1.77, 22.21) * mm, "end": v(10.76, 22.21) * mm});
            skLineSegment(sketch, "E107.top", {"start": v(-1.77, 26.45) * mm, "end": v(10.76, 26.45) * mm});
            skLineSegment(sketch, "E107.left", {"start": v(-1.77, 22.21) * mm, "end": v(-1.77, 26.45) * mm});
            skLineSegment(sketch, "E107.right", {"start": v(10.76, 22.21) * mm, "end": v(10.76, 26.45) * mm});
            skSolve(sketch);
        }
        {
            var Q0;
            Q0=qCreatedBy(makeId("Top.planeOp"),FACE);
            var sketch = newSketch(context, id + "F6", { "sketchPlane" : qUnion([Q0])});
            skLineSegment(sketch, "E108.bottom", {"start": v(44.27, 9.68) * mm, "end": v(56.64, 9.68) * mm});
            skLineSegment(sketch, "E108.top", {"start": v(44.27, 5.24) * mm, "end": v(56.64, 5.24) * mm});
            skLineSegment(sketch, "E108.left", {"start": v(44.27, 9.68) * mm, "end": v(44.27, 5.24) * mm});
            skLineSegment(sketch, "E108.right", {"start": v(56.64, 9.68) * mm, "end": v(56.64, 5.24) * mm});
            skLineSegment(sketch, "E109.bottom", {"start": v(61.11, 5.27) * mm, "end": v(65.46, 5.27) * mm});
            skLineSegment(sketch, "E109.top", {"start": v(61.11, 9.65) * mm, "end": v(65.46, 9.65) * mm});
            skLineSegment(sketch, "E109.left", {"start": v(61.11, 5.27) * mm, "end": v(61.11, 9.65) * mm});
            skLineSegment(sketch, "E109.right", {"start": v(65.46, 5.27) * mm, "end": v(65.46, 9.65) * mm});
            skLineSegment(sketch, "E110.bottom", {"start": v(-5.96, -32.3) * mm, "end": v(6.62, -32.3) * mm});
            skLineSegment(sketch, "E110.top", {"start": v(-5.96, -28.1) * mm, "end": v(6.62, -28.1) * mm});
            skLineSegment(sketch, "E110.left", {"start": v(-5.96, -32.3) * mm, "end": v(-5.96, -28.1) * mm});
            skLineSegment(sketch, "E110.right", {"start": v(6.62, -32.3) * mm, "end": v(6.62, -28.1) * mm});
            skLineSegment(sketch, "E111.bottom", {"start": v(-1.74, -28.1) * mm, "end": v(10.73, -28.1) * mm});
            skLineSegment(sketch, "E111.top", {"start": v(-1.74, -24.13) * mm, "end": v(10.73, -24.13) * mm});
            skLineSegment(sketch, "E111.left", {"start": v(-1.74, -28.1) * mm, "end": v(-1.74, -24.13) * mm});
            skLineSegment(sketch, "E111.right", {"start": v(10.73, -28.1) * mm, "end": v(10.73, -24.13) * mm});
            skLineSegment(sketch, "E112.bottom", {"start": v(6.62, -24.13) * mm, "end": v(2.37, -24.13) * mm});
            skLineSegment(sketch, "E112.top", {"start": v(6.62, -19.84) * mm, "end": v(2.37, -19.84) * mm});
            skLineSegment(sketch, "E112.left", {"start": v(6.62, -24.13) * mm, "end": v(6.62, -19.84) * mm});
            skLineSegment(sketch, "E112.right", {"start": v(2.37, -24.13) * mm, "end": v(2.37, -19.84) * mm});
            skLineSegment(sketch, "E113.bottom", {"start": v(-18.67, -36.76) * mm, "end": v(-26.9, -36.76) * mm});
            skLineSegment(sketch, "E113.top", {"start": v(-18.67, -24.13) * mm, "end": v(-26.9, -24.13) * mm});
            skLineSegment(sketch, "E113.left", {"start": v(-18.67, -36.76) * mm, "end": v(-18.67, -24.13) * mm});
            skLineSegment(sketch, "E113.right", {"start": v(-26.9, -36.76) * mm, "end": v(-26.9, -24.13) * mm});
            skLineSegment(sketch, "E114.bottom", {"start": v(-26.9, -24.13) * mm, "end": v(-31.16, -24.13) * mm});
            skLineSegment(sketch, "E114.top", {"start": v(-26.9, -32.32) * mm, "end": v(-31.16, -32.32) * mm});
            skLineSegment(sketch, "E114.left", {"start": v(-26.9, -24.13) * mm, "end": v(-26.9, -32.32) * mm});
            skLineSegment(sketch, "E114.right", {"start": v(-31.16, -24.13) * mm, "end": v(-31.16, -32.32) * mm});
            skLineSegment(sketch, "E115.bottom", {"start": v(-18.67, -32.36) * mm, "end": v(-14.33, -32.36) * mm});
            skLineSegment(sketch, "E115.top", {"start": v(-18.67, -28.16) * mm, "end": v(-14.33, -28.16) * mm});
            skLineSegment(sketch, "E115.left", {"start": v(-18.67, -32.36) * mm, "end": v(-18.67, -28.16) * mm});
            skLineSegment(sketch, "E115.right", {"start": v(-14.33, -32.36) * mm, "end": v(-14.33, -28.16) * mm});
            skLineSegment(sketch, "E116.bottom", {"start": v(-22.79, -24.13) * mm, "end": v(-26.82, -24.13) * mm});
            skLineSegment(sketch, "E116.top", {"start": v(-22.79, -19.83) * mm, "end": v(-26.82, -19.83) * mm});
            skLineSegment(sketch, "E116.left", {"start": v(-22.79, -24.13) * mm, "end": v(-22.79, -19.83) * mm});
            skLineSegment(sketch, "E116.right", {"start": v(-26.82, -24.13) * mm, "end": v(-26.82, -19.83) * mm});
            skLineSegment(sketch, "E117.bottom", {"start": v(19.08, 30.43) * mm, "end": v(10.81, 30.43) * mm});
            skLineSegment(sketch, "E117.top", {"start": v(19.08, 34.86) * mm, "end": v(10.81, 34.86) * mm});
            skLineSegment(sketch, "E117.left", {"start": v(19.08, 30.43) * mm, "end": v(19.08, 34.86) * mm});
            skLineSegment(sketch, "E117.right", {"start": v(10.81, 30.43) * mm, "end": v(10.81, 34.86) * mm});
            skLineSegment(sketch, "E118.bottom", {"start": v(35.8, -3.1) * mm, "end": v(27.68, -3.1) * mm});
            skLineSegment(sketch, "E118.top", {"start": v(35.8, 9.62) * mm, "end": v(27.68, 9.62) * mm});
            skLineSegment(sketch, "E118.left", {"start": v(35.8, -3.1) * mm, "end": v(35.8, 9.62) * mm});
            skLineSegment(sketch, "E118.right", {"start": v(27.68, -3.1) * mm, "end": v(27.68, 9.62) * mm});
            skLineSegment(sketch, "E119.bottom", {"start": v(27.68, -3.1) * mm, "end": v(19.1, -3.1) * mm});
            skLineSegment(sketch, "E119.top", {"start": v(27.68, 5.25) * mm, "end": v(19.1, 5.25) * mm});
            skLineSegment(sketch, "E119.left", {"start": v(27.68, -3.1) * mm, "end": v(27.68, 5.25) * mm});
            skLineSegment(sketch, "E119.right", {"start": v(19.1, -3.1) * mm, "end": v(19.1, 5.25) * mm});
            skLineSegment(sketch, "E120.bottom", {"start": v(19.1, -3.1) * mm, "end": v(14.9, -3.1) * mm});
            skLineSegment(sketch, "E120.top", {"start": v(19.1, 0.97) * mm, "end": v(14.9, 0.97) * mm});
            skLineSegment(sketch, "E120.left", {"start": v(19.1, -3.1) * mm, "end": v(19.1, 0.97) * mm});
            skLineSegment(sketch, "E120.right", {"start": v(14.9, -3.1) * mm, "end": v(14.9, 0.97) * mm});
            skLineSegment(sketch, "E121.bottom", {"start": v(2.42, 47.14) * mm, "end": v(10.81, 47.14) * mm});
            skLineSegment(sketch, "E121.top", {"start": v(2.42, 43.13) * mm, "end": v(10.81, 43.13) * mm});
            skLineSegment(sketch, "E121.left", {"start": v(2.42, 47.14) * mm, "end": v(2.42, 43.13) * mm});
            skLineSegment(sketch, "E121.right", {"start": v(10.81, 47.14) * mm, "end": v(10.81, 43.13) * mm});
            skLineSegment(sketch, "E122.bottom", {"start": v(6.62, 43.13) * mm, "end": v(15.07, 43.13) * mm});
            skLineSegment(sketch, "E122.top", {"start": v(6.62, 38.69) * mm, "end": v(15.07, 38.69) * mm});
            skLineSegment(sketch, "E122.left", {"start": v(6.62, 43.13) * mm, "end": v(6.62, 38.69) * mm});
            skLineSegment(sketch, "E122.right", {"start": v(15.07, 43.13) * mm, "end": v(15.07, 38.69) * mm});
            skLineSegment(sketch, "E123.bottom", {"start": v(-14.28, 17.83) * mm, "end": v(-18.64, 17.83) * mm});
            skLineSegment(sketch, "E123.top", {"start": v(-14.28, 30.43) * mm, "end": v(-18.64, 30.43) * mm});
            skLineSegment(sketch, "E123.left", {"start": v(-14.28, 17.83) * mm, "end": v(-14.28, 30.43) * mm});
            skLineSegment(sketch, "E123.right", {"start": v(-18.64, 17.83) * mm, "end": v(-18.64, 30.43) * mm});
            skLineSegment(sketch, "E124.bottom", {"start": v(-39.51, 17.85) * mm, "end": v(-18.67, 17.85) * mm});
            skLineSegment(sketch, "E124.top", {"start": v(-39.51, 9.64) * mm, "end": v(-18.67, 9.64) * mm});
            skLineSegment(sketch, "E124.left", {"start": v(-39.51, 17.85) * mm, "end": v(-39.51, 9.64) * mm});
            skLineSegment(sketch, "E124.right", {"start": v(-18.67, 17.85) * mm, "end": v(-18.67, 9.64) * mm});
            skLineSegment(sketch, "E125.bottom", {"start": v(-31.17, 17.85) * mm, "end": v(-22.79, 17.85) * mm});
            skLineSegment(sketch, "E125.top", {"start": v(-31.17, 22.19) * mm, "end": v(-22.79, 22.19) * mm});
            skLineSegment(sketch, "E125.left", {"start": v(-31.17, 17.85) * mm, "end": v(-31.17, 22.19) * mm});
            skLineSegment(sketch, "E125.right", {"start": v(-22.79, 17.85) * mm, "end": v(-22.79, 22.19) * mm});
            skLineSegment(sketch, "E126.bottom", {"start": v(-31.15, 9.64) * mm, "end": v(-26.9, 9.64) * mm});
            skLineSegment(sketch, "E126.top", {"start": v(-31.15, 5.25) * mm, "end": v(-26.9, 5.25) * mm});
            skLineSegment(sketch, "E126.left", {"start": v(-31.15, 9.64) * mm, "end": v(-31.15, 5.25) * mm});
            skLineSegment(sketch, "E126.right", {"start": v(-26.9, 9.64) * mm, "end": v(-26.9, 5.25) * mm});
            skLineSegment(sketch, "E127.bottom", {"start": v(-22.79, 9.64) * mm, "end": v(-14.33, 9.64) * mm});
            skLineSegment(sketch, "E127.top", {"start": v(-22.79, 5.25) * mm, "end": v(-14.33, 5.25) * mm});
            skLineSegment(sketch, "E127.left", {"start": v(-22.79, 9.64) * mm, "end": v(-22.79, 5.25) * mm});
            skLineSegment(sketch, "E127.right", {"start": v(-14.33, 9.64) * mm, "end": v(-14.33, 5.25) * mm});
            skLineSegment(sketch, "E128.bottom", {"start": v(-18.56, 5.25) * mm, "end": v(-10.05, 5.25) * mm});
            skLineSegment(sketch, "E128.top", {"start": v(-18.56, 0.97) * mm, "end": v(-10.05, 0.97) * mm});
            skLineSegment(sketch, "E128.left", {"start": v(-18.56, 5.25) * mm, "end": v(-18.56, 0.97) * mm});
            skLineSegment(sketch, "E128.right", {"start": v(-10.05, 5.25) * mm, "end": v(-10.05, 0.97) * mm});
            skLineSegment(sketch, "E129.bottom", {"start": v(-14.3, 0.97) * mm, "end": v(-5.96, 0.97) * mm});
            skLineSegment(sketch, "E129.top", {"start": v(-14.3, -15.53) * mm, "end": v(-5.96, -15.53) * mm});
            skLineSegment(sketch, "E129.left", {"start": v(-14.3, 0.97) * mm, "end": v(-14.3, -15.53) * mm});
            skLineSegment(sketch, "E129.right", {"start": v(-5.96, 0.97) * mm, "end": v(-5.96, -15.53) * mm});
            skLineSegment(sketch, "E130.bottom", {"start": v(-5.96, -15.53) * mm, "end": v(6.62, -15.53) * mm});
            skLineSegment(sketch, "E130.top", {"start": v(-5.96, -3.1) * mm, "end": v(6.62, -3.1) * mm});
            skLineSegment(sketch, "E130.left", {"start": v(-5.96, -15.53) * mm, "end": v(-5.96, -3.1) * mm});
            skLineSegment(sketch, "E130.right", {"start": v(6.62, -15.53) * mm, "end": v(6.62, -3.1) * mm});
            skLineSegment(sketch, "E131.bottom", {"start": v(14.9, -3.1) * mm, "end": v(6.62, -3.1) * mm});
            skLineSegment(sketch, "E131.top", {"start": v(14.9, -7.27) * mm, "end": v(6.62, -7.27) * mm});
            skLineSegment(sketch, "E131.left", {"start": v(14.9, -3.1) * mm, "end": v(14.9, -7.27) * mm});
            skLineSegment(sketch, "E131.right", {"start": v(6.62, -3.1) * mm, "end": v(6.62, -7.27) * mm});
            skLineSegment(sketch, "E132.bottom", {"start": v(6.62, -7.27) * mm, "end": v(10.8, -7.27) * mm});
            skLineSegment(sketch, "E132.top", {"start": v(6.62, -11.37) * mm, "end": v(10.8, -11.37) * mm});
            skLineSegment(sketch, "E132.left", {"start": v(6.62, -7.27) * mm, "end": v(6.62, -11.37) * mm});
            skLineSegment(sketch, "E132.right", {"start": v(10.8, -7.27) * mm, "end": v(10.8, -11.37) * mm});
            skLineSegment(sketch, "E133.bottom", {"start": v(-14.3, -11.48) * mm, "end": v(-18.54, -11.48) * mm});
            skLineSegment(sketch, "E133.top", {"start": v(-14.3, -7.28) * mm, "end": v(-18.54, -7.28) * mm});
            skLineSegment(sketch, "E133.left", {"start": v(-14.3, -11.48) * mm, "end": v(-14.3, -7.28) * mm});
            skLineSegment(sketch, "E133.right", {"start": v(-18.54, -11.48) * mm, "end": v(-18.54, -7.28) * mm});
            skSolve(sketch);
        }
        {
            var Q0;
            Q0 = qSketchRegion(id + "F5", true);
            extrude(context, id + "F7", {"entities" : qUnion([Q0]), "depth" : 6.35 * mm, "offsetDistance" : 25.4 * mm});
        }
        {
            var Q0;
            {var subQ4=sQuery(id+"F4.wireOp",EDGE,"E101.bottom");var subQ6=sQuery(id+"F4.wireOp",EDGE,"E100.top");Q0=qUnion([makeQuery(id+"F4.imprint","IMPRINT",FACE,{"disambiguationData":[TD([[makeQuery(id+"F4.imprint","IMPRINT",EDGE,{"derivedFrom":sQuery(id+"F4.wireOp",EDGE,"E96.bottom")}),-1.0]])]}),makeQuery(id+"F4.imprint","IMPRINT",FACE,{"disambiguationData":[TD([[makeQuery(id+"F4.imprint","IMPRINT",EDGE,{"derivedFrom":sQuery(id+"F4.wireOp",EDGE,"E97.bottom")}),1.0]])]}),makeQuery(id+"F4.imprint","IMPRINT",FACE,{"disambiguationData":[TD([[makeQuery(id+"F4.imprint","IMPRINT",EDGE,{"derivedFrom":sQuery(id+"F4.wireOp",EDGE,"E98.bottom")}),-1.0]])]}),makeQuery(id+"F4.imprint","IMPRINT",FACE,{"disambiguationData":[TD([[makeQuery(id+"F4.imprint","IMPRINT",EDGE,{"derivedFrom":sQuery(id+"F4.wireOp",EDGE,"E102.bottom")}),1.0]])]}),makeQuery(id+"F4.imprint","IMPRINT",FACE,{"disambiguationData":[TD([[makeQuery(id+"F4.imprint","IMPRINT",EDGE,{"derivedFrom":sQuery(id+"F4.wireOp",EDGE,"E99.top")}),-1.0]])]}),makeQuery(id+"F4.imprint","IMPRINT",FACE,{"disambiguationData":[TD([[makeQuery(id+"F4.imprint","IMPRINT",EDGE,{"derivedFrom":subQ4}),-1.0]])]}),makeQuery(id+"F4.imprint","IMPRINT",FACE,{"disambiguationData":[TD([[makeQuery(id+"F4.imprint","IMPRINT",EDGE,{"derivedFrom":subQ6}),1.0]])]})]);}
            extrude(context, id + "F8", {"entities" : qUnion([Q0]), "depth" : 5.08 * mm, "offsetDistance" : 25.4 * mm});
        }
        {
            var Q0;
            {var subQ0=sQuery(id+"F6.wireOp",EDGE,"E122.bottom");var subQ7=sQuery(id+"F6.wireOp",EDGE,"E131.bottom");var subQ13=sQuery(id+"F6.wireOp",EDGE,"E130.bottom");var subQ18=sQuery(id+"F6.wireOp",EDGE,"E132.top");var subQ26=sQuery(id+"F6.wireOp",EDGE,"E129.bottom");var subQ29=sQuery(id+"F6.wireOp",EDGE,"E133.bottom");var subQ32=sQuery(id+"F6.wireOp",EDGE,"E124.left");var subQ48=sQuery(id+"F6.wireOp",EDGE,"E127.bottom");var subQ55=sQuery(id+"F6.wireOp",EDGE,"E128.bottom");var subQ64=sQuery(id+"F6.wireOp",EDGE,"E119.bottom");var subQ66=sQuery(id+"F6.wireOp",EDGE,"E118.bottom");var subQ69=sQuery(id+"F6.wireOp",EDGE,"E120.bottom");var subQ72=sQuery(id+"F6.wireOp",EDGE,"E115.bottom");var subQ78=sQuery(id+"F6.wireOp",EDGE,"E114.bottom");var subQ88=sQuery(id+"F6.wireOp",EDGE,"E113.bottom");var subQ96=sQuery(id+"F6.wireOp",EDGE,"E111.bottom");Q0=qUnion([makeQuery(id+"F6.imprint","IMPRINT",FACE,{"disambiguationData":[TD([[makeQuery(id+"F6.imprint","IMPRINT",EDGE,{"derivedFrom":sQuery(id+"F6.wireOp",EDGE,"E108.bottom")}),-1.0]])]}),makeQuery(id+"F6.imprint","IMPRINT",FACE,{"disambiguationData":[TD([[makeQuery(id+"F6.imprint","IMPRINT",EDGE,{"derivedFrom":sQuery(id+"F6.wireOp",EDGE,"E109.bottom")}),1.0]])]}),makeQuery(id+"F6.imprint","IMPRINT",FACE,{"disambiguationData":[TD([[makeQuery(id+"F6.imprint","IMPRINT",EDGE,{"derivedFrom":sQuery(id+"F6.wireOp",EDGE,"E117.bottom")}),-1.0]])]}),makeQuery(id+"F6.imprint","IMPRINT",FACE,{"disambiguationData":[TD([[makeQuery(id+"F6.imprint","IMPRINT",EDGE,{"derivedFrom":sQuery(id+"F6.wireOp",EDGE,"E123.bottom")}),-1.0]])]}),makeQuery(id+"F6.imprint","IMPRINT",FACE,{"disambiguationData":[TD([[makeQuery(id+"F6.imprint","IMPRINT",EDGE,{"derivedFrom":sQuery(id+"F6.wireOp",EDGE,"E110.bottom")}),1.0]])]}),makeQuery(id+"F6.imprint","IMPRINT",FACE,{"disambiguationData":[TD([[makeQuery(id+"F6.imprint","IMPRINT",EDGE,{"derivedFrom":sQuery(id+"F6.wireOp",EDGE,"E112.top")}),1.0]])]}),makeQuery(id+"F6.imprint","IMPRINT",FACE,{"disambiguationData":[TD([[makeQuery(id+"F6.imprint","IMPRINT",EDGE,{"derivedFrom":subQ96}),1.0]])]}),makeQuery(id+"F6.imprint","IMPRINT",FACE,{"disambiguationData":[TD([[makeQuery(id+"F6.imprint","IMPRINT",EDGE,{"derivedFrom":subQ78}),1.0]])]}),makeQuery(id+"F6.imprint","IMPRINT",FACE,{"disambiguationData":[TD([[makeQuery(id+"F6.imprint","IMPRINT",EDGE,{"derivedFrom":sQuery(id+"F6.wireOp",EDGE,"E116.top")}),1.0]])]}),makeQuery(id+"F6.imprint","IMPRINT",FACE,{"disambiguationData":[TD([[makeQuery(id+"F6.imprint","IMPRINT",EDGE,{"derivedFrom":subQ88}),-1.0]])]}),makeQuery(id+"F6.imprint","IMPRINT",FACE,{"disambiguationData":[TD([[makeQuery(id+"F6.imprint","IMPRINT",EDGE,{"derivedFrom":subQ72}),1.0]])]}),makeQuery(id+"F6.imprint","IMPRINT",FACE,{"disambiguationData":[TD([[makeQuery(id+"F6.imprint","IMPRINT",EDGE,{"derivedFrom":subQ66}),-1.0]])]}),makeQuery(id+"F6.imprint","IMPRINT",FACE,{"disambiguationData":[TD([[makeQuery(id+"F6.imprint","IMPRINT",EDGE,{"derivedFrom":subQ69}),-1.0]])]}),makeQuery(id+"F6.imprint","IMPRINT",FACE,{"disambiguationData":[TD([[makeQuery(id+"F6.imprint","IMPRINT",EDGE,{"derivedFrom":sQuery(id+"F6.wireOp",EDGE,"E125.top")}),-1.0]])]}),makeQuery(id+"F6.imprint","IMPRINT",FACE,{"disambiguationData":[TD([[makeQuery(id+"F6.imprint","IMPRINT",EDGE,{"derivedFrom":sQuery(id+"F6.wireOp",EDGE,"E126.top")}),1.0]])]}),makeQuery(id+"F6.imprint","IMPRINT",FACE,{"disambiguationData":[TD([[makeQuery(id+"F6.imprint","IMPRINT",EDGE,{"derivedFrom":subQ29}),-1.0]])]}),makeQuery(id+"F6.imprint","IMPRINT",FACE,{"disambiguationData":[TD([[makeQuery(id+"F6.imprint","IMPRINT",EDGE,{"derivedFrom":subQ64}),-1.0]])]}),makeQuery(id+"F6.imprint","IMPRINT",FACE,{"disambiguationData":[TD([[makeQuery(id+"F6.imprint","IMPRINT",EDGE,{"derivedFrom":subQ48}),-1.0]])]}),makeQuery(id+"F6.imprint","IMPRINT",FACE,{"disambiguationData":[TD([[makeQuery(id+"F6.imprint","IMPRINT",EDGE,{"derivedFrom":subQ55}),-1.0]])]}),makeQuery(id+"F6.imprint","IMPRINT",FACE,{"disambiguationData":[TD([[makeQuery(id+"F6.imprint","IMPRINT",EDGE,{"derivedFrom":subQ7}),1.0]])]}),makeQuery(id+"F6.imprint","IMPRINT",FACE,{"disambiguationData":[TD([[makeQuery(id+"F6.imprint","IMPRINT",EDGE,{"derivedFrom":subQ18}),1.0]])]}),makeQuery(id+"F6.imprint","IMPRINT",FACE,{"disambiguationData":[TD([[makeQuery(id+"F6.imprint","IMPRINT",EDGE,{"derivedFrom":subQ32}),1.0]])]}),makeQuery(id+"F6.imprint","IMPRINT",FACE,{"disambiguationData":[TD([[makeQuery(id+"F6.imprint","IMPRINT",EDGE,{"derivedFrom":subQ26}),-1.0]])]}),makeQuery(id+"F6.imprint","IMPRINT",FACE,{"disambiguationData":[TD([[makeQuery(id+"F6.imprint","IMPRINT",EDGE,{"derivedFrom":subQ13}),1.0]])]}),makeQuery(id+"F6.imprint","IMPRINT",FACE,{"disambiguationData":[TD([[makeQuery(id+"F6.imprint","IMPRINT",EDGE,{"derivedFrom":sQuery(id+"F6.wireOp",EDGE,"E121.bottom")}),-1.0]])]}),makeQuery(id+"F6.imprint","IMPRINT",FACE,{"disambiguationData":[TD([[makeQuery(id+"F6.imprint","IMPRINT",EDGE,{"derivedFrom":subQ0}),-1.0]])]})]);}
            extrude(context, id + "F9", {"entities" : qUnion([Q0]), "depth" : 2.54 * mm, "offsetDistance" : 25.4 * mm});
        }
        {
            var Q0;
            Q0=makeQuery(id+"F1.opExtrude","CAP_FACE",FACE,{"disambiguationData":[OSD([sQuery(id+"F0.wireOp",EDGE,"E61.bottom"),sQuery(id+"F0.wireOp",EDGE,"E61.top"),sQuery(id+"F0.wireOp",EDGE,"E61.left"),sQuery(id+"F0.wireOp",EDGE,"E61.right")])],"isStart":false});
            var Q1;
            Q1=makeQuery(id+"F1.opExtrude","CAP_FACE",FACE,{"disambiguationData":[OSD([sQuery(id+"F0.wireOp",EDGE,"E62.bottom"),sQuery(id+"F0.wireOp",EDGE,"E62.top"),sQuery(id+"F0.wireOp",EDGE,"E62.left"),sQuery(id+"F0.wireOp",EDGE,"E62.right")])],"isStart":false});
            var Q2;
            Q2=makeQuery(id+"F1.opExtrude","CAP_FACE",FACE,{"disambiguationData":[OSD([sQuery(id+"F0.wireOp",EDGE,"E63.bottom"),sQuery(id+"F0.wireOp",EDGE,"E63.top"),sQuery(id+"F0.wireOp",EDGE,"E63.left"),sQuery(id+"F0.wireOp",EDGE,"E63.right")])],"isStart":false});
            var Q3;
            Q3=makeQuery(id+"F1.opExtrude","CAP_FACE",FACE,{"disambiguationData":[OSD([sQuery(id+"F0.wireOp",EDGE,"E4.bottom"),sQuery(id+"F0.wireOp",EDGE,"E4.top"),sQuery(id+"F0.wireOp",EDGE,"E4.left"),sQuery(id+"F0.wireOp",EDGE,"E4.right"),sQuery(id+"F0.wireOp",EDGE,"E5.bottom"),sQuery(id+"F0.wireOp",EDGE,"E5.top"),sQuery(id+"F0.wireOp",EDGE,"E5.right"),sQuery(id+"F0.wireOp",EDGE,"E11.bottom"),sQuery(id+"F0.wireOp",EDGE,"E11.left"),sQuery(id+"F0.wireOp",EDGE,"E11.right"),sQuery(id+"F0.wireOp",EDGE,"E59.bottom"),sQuery(id+"F0.wireOp",EDGE,"E59.top"),sQuery(id+"F0.wireOp",EDGE,"E59.left"),sQuery(id+"F0.wireOp",EDGE,"E59.right")])],"isStart":false});
            var Q4;
            Q4=makeQuery(id+"F1.opExtrude","CAP_FACE",FACE,{"disambiguationData":[OSD([sQuery(id+"F0.wireOp",EDGE,"E57.bottom"),sQuery(id+"F0.wireOp",EDGE,"E57.top"),sQuery(id+"F0.wireOp",EDGE,"E57.left"),sQuery(id+"F0.wireOp",EDGE,"E57.right")])],"isStart":false});
            var Q5;
            Q5=makeQuery(id+"F1.opExtrude","CAP_FACE",FACE,{"disambiguationData":[OSD([sQuery(id+"F0.wireOp",EDGE,"E58.bottom"),sQuery(id+"F0.wireOp",EDGE,"E58.top"),sQuery(id+"F0.wireOp",EDGE,"E58.left"),sQuery(id+"F0.wireOp",EDGE,"E58.right")])],"isStart":false});
            extrude(context, id + "F10", {"entities" : qUnion([Q0, Q1, Q2, Q3, Q4, Q5]), "depth" : 2.3 * mm, "offsetDistance" : 25.4 * mm});
        }
    });
